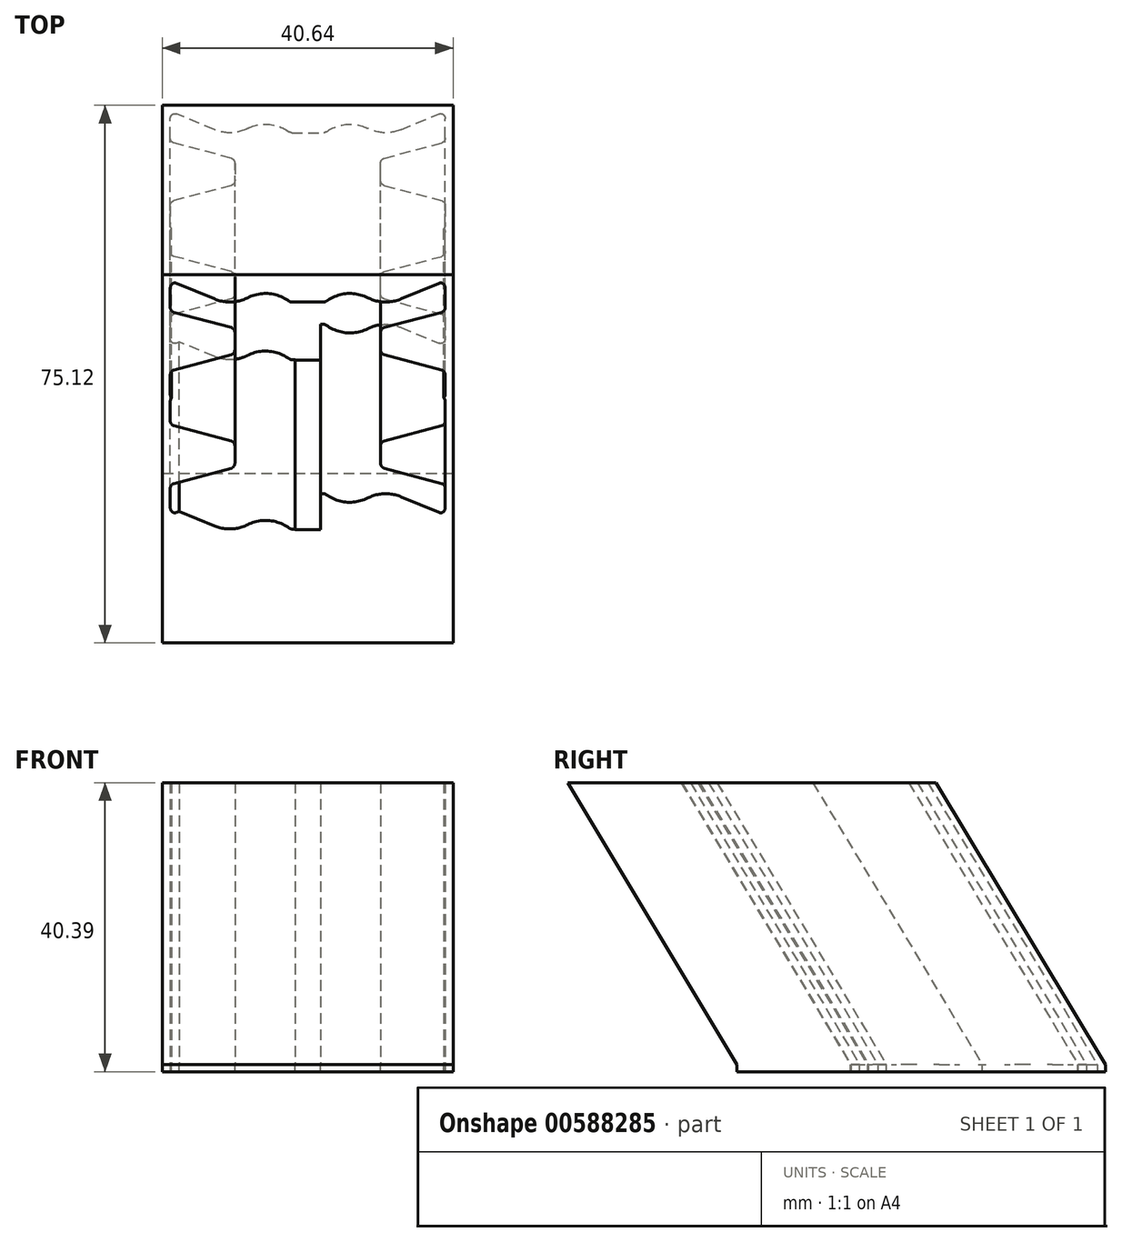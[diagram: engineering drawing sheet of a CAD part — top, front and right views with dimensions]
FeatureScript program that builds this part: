
annotation { "Feature Type Name" : "Feature", "Feature Type Description" : "" }
export const myFeature = defineFeature(function(context is Context, id is Id, definition is map)
    precondition{}
    {
        {
            var Q0;
            Q0=qCreatedBy(makeId("Front.planeOp"),FACE);
            var sketch = newSketch(context, id + "F0", { "sketchPlane" : qUnion([Q0])});
            skLineSegment(sketch, "E0.left", {"start": v(10.18, 1.51) * mm, "end": v(10.18, 0) * mm});
            skLineSegment(sketch, "E1", {"start": v(18.72, 3.46) * mm, "end": v(10.67, 1.62) * mm});
            skLineSegment(sketch, "E2.left", {"start": v(19.2, 6.35) * mm, "end": v(19.22, 4.09) * mm});
            skLineSegment(sketch, "E3", {"start": v(10.18, 1) * mm, "end": v(10.18, 0) * mm});
            skLineSegment(sketch, "E4", {"start": v(18.36, 6.94) * mm, "end": v(13.01, 5.05) * mm});
            skLineSegment(sketch, "E5", {"start": v(1.78, -8.98) * mm, "end": v(1.78, -4.68) * mm});
            skArc(sketch, "E6", {"start": v(8.39, 5.2) * mm, "mid": v(5.43, 5.7) * mm, "end": v(2.57, 4.77) * mm});
            skLineSegment(sketch, "E7", {"start": v(2.42, 4.68) * mm, "end": v(2.42, 4.68) * mm});
            skLineSegment(sketch, "E8.MirrorCS", {"start": v(-1.78, -8.98) * mm, "end": v(-1.78, -4.68) * mm});
            skLineSegment(sketch, "E9", {"start": v(-1.78, -8.98) * mm, "end": v(1.78, -8.98) * mm});
            skPoint(sketch, "E10.visualSharp", {"position": v(10.18, 4.04) * mm});
            skArc(sketch, "E10.filletArc", {"start": v(8.39, 5.2) * mm, "mid": v(10.69, 4.69) * mm, "end": v(13.01, 5.05) * mm});
            skLineSegment(sketch, "E11", {"start": v(0, 4.68) * mm, "end": v(2.23, 4.68) * mm});
            skPoint(sketch, "E12.visualSharp", {"position": v(19.2, 7.24) * mm});
            skArc(sketch, "E12.filletArc", {"start": v(19.2, 6.35) * mm, "mid": v(18.93, 6.86) * mm, "end": v(18.36, 6.94) * mm});
            skPoint(sketch, "E13.visualSharp", {"position": v(19.22, 3.58) * mm});
            skArc(sketch, "E13.filletArc", {"start": v(18.72, 3.46) * mm, "mid": v(19.08, 3.69) * mm, "end": v(19.22, 4.09) * mm});
            skPoint(sketch, "E14.visualSharp", {"position": v(10.18, 1.51) * mm});
            skArc(sketch, "E14.filletArc", {"start": v(10.67, 1.62) * mm, "mid": v(10.31, 1.4) * mm, "end": v(10.18, 1) * mm});
            skPoint(sketch, "E15.visualSharp", {"position": v(2.42, 4.68) * mm});
            skArc(sketch, "E15.filletArc", {"start": v(2.23, 4.68) * mm, "mid": v(2.4, 4.7) * mm, "end": v(2.57, 4.77) * mm});
            skArc(sketch, "E16.MirrorCS", {"start": v(-2.23, 4.68) * mm, "mid": v(-2.4, 4.7) * mm, "end": v(-2.57, 4.77) * mm});
            skLineSegment(sketch, "E17.MirrorCS", {"start": v(-10.18, 1) * mm, "end": v(-10.18, 0) * mm});
            skArc(sketch, "E18.MirrorCS", {"start": v(-10.67, 1.62) * mm, "mid": v(-10.31, 1.4) * mm, "end": v(-10.18, 1) * mm});
            skLineSegment(sketch, "E19.MirrorCS", {"start": v(-19.2, 6.35) * mm, "end": v(-19.22, 4.09) * mm});
            skArc(sketch, "E20.MirrorCS", {"start": v(-18.72, 3.46) * mm, "mid": v(-19.08, 3.69) * mm, "end": v(-19.22, 4.09) * mm});
            skLineSegment(sketch, "E21.MirrorCS", {"start": v(-10.18, 1.51) * mm, "end": v(-10.18, 0) * mm});
            skArc(sketch, "E22.MirrorCS", {"start": v(-19.2, 6.35) * mm, "mid": v(-18.93, 6.86) * mm, "end": v(-18.36, 6.94) * mm});
            skLineSegment(sketch, "E23.MirrorCS", {"start": v(0, 4.68) * mm, "end": v(-2.23, 4.68) * mm});
            skArc(sketch, "E24.MirrorCS", {"start": v(-8.39, 5.2) * mm, "mid": v(-10.69, 4.69) * mm, "end": v(-13.01, 5.05) * mm});
            skPoint(sketch, "E25.MirrorP", {"position": v(-2.42, 4.68) * mm});
            skArc(sketch, "E26.MirrorCS", {"start": v(-8.39, 5.2) * mm, "mid": v(-5.43, 5.7) * mm, "end": v(-2.57, 4.77) * mm});
            skLineSegment(sketch, "E27.MirrorCS", {"start": v(-18.72, 3.46) * mm, "end": v(-10.67, 1.62) * mm});
            skLineSegment(sketch, "E28.MirrorCS", {"start": v(-18.36, 6.94) * mm, "end": v(-13.01, 5.05) * mm});
            skPoint(sketch, "E29.MirrorP", {"position": v(-19.22, 3.58) * mm});
            skPoint(sketch, "E30.MirrorP", {"position": v(-10.18, 1.51) * mm});
            skPoint(sketch, "E31.MirrorP", {"position": v(-10.18, 4.04) * mm});
            skPoint(sketch, "E32.MirrorP", {"position": v(-19.2, 7.24) * mm});
            skLineSegment(sketch, "E33.MirrorCS", {"start": v(-2.42, 4.68) * mm, "end": v(-2.42, 4.68) * mm});
            skLineSegment(sketch, "E34.MirrorCS", {"start": v(10.18, -1.51) * mm, "end": v(10.18, 0) * mm});
            skArc(sketch, "E35.MirrorCS", {"start": v(2.23, -4.68) * mm, "mid": v(2.4, -4.7) * mm, "end": v(2.57, -4.77) * mm});
            skLineSegment(sketch, "E36.MirrorCS", {"start": v(-10.18, -1) * mm, "end": v(-10.18, 0) * mm});
            skArc(sketch, "E37.MirrorCS", {"start": v(-2.23, -4.68) * mm, "mid": v(-2.4, -4.7) * mm, "end": v(-2.57, -4.77) * mm});
            skLineSegment(sketch, "E38.MirrorCS", {"start": v(-19.2, -6.35) * mm, "end": v(-19.22, -4.09) * mm});
            skArc(sketch, "E39.MirrorCS", {"start": v(19.2, -6.35) * mm, "mid": v(18.93, -6.86) * mm, "end": v(18.36, -6.94) * mm});
            skArc(sketch, "E40.MirrorCS", {"start": v(-18.72, -3.46) * mm, "mid": v(-19.08, -3.69) * mm, "end": v(-19.22, -4.09) * mm});
            skLineSegment(sketch, "E41.MirrorCS", {"start": v(10.18, -1) * mm, "end": v(10.18, 0) * mm});
            skArc(sketch, "E42.MirrorCS", {"start": v(10.67, -1.62) * mm, "mid": v(10.31, -1.4) * mm, "end": v(10.18, -1) * mm});
            skLineSegment(sketch, "E43.MirrorCS", {"start": v(19.2, -6.35) * mm, "end": v(19.22, -4.09) * mm});
            skArc(sketch, "E44.MirrorCS", {"start": v(18.72, -3.46) * mm, "mid": v(19.08, -3.69) * mm, "end": v(19.22, -4.09) * mm});
            skArc(sketch, "E45.MirrorCS", {"start": v(-19.2, -6.35) * mm, "mid": v(-18.93, -6.86) * mm, "end": v(-18.36, -6.94) * mm});
            skLineSegment(sketch, "E46.MirrorCS", {"start": v(-10.18, -1.51) * mm, "end": v(-10.18, 0) * mm});
            skArc(sketch, "E47.MirrorCS", {"start": v(-10.67, -1.62) * mm, "mid": v(-10.31, -1.4) * mm, "end": v(-10.18, -1) * mm});
            skLineSegment(sketch, "E48.MirrorCS", {"start": v(1.78, -4.68) * mm, "end": v(2.23, -4.68) * mm});
            skLineSegment(sketch, "E49.MirrorCS", {"start": v(-1.78, -4.68) * mm, "end": v(-2.23, -4.68) * mm});
            skArc(sketch, "E50.MirrorCS", {"start": v(8.39, -5.2) * mm, "mid": v(10.69, -4.69) * mm, "end": v(13.01, -5.05) * mm});
            skArc(sketch, "E51.MirrorCS", {"start": v(-8.39, -5.2) * mm, "mid": v(-10.69, -4.69) * mm, "end": v(-13.01, -5.05) * mm});
            skPoint(sketch, "E52.MirrorP", {"position": v(-2.42, -4.68) * mm});
            skArc(sketch, "E53.MirrorCS", {"start": v(8.39, -5.2) * mm, "mid": v(5.43, -5.7) * mm, "end": v(2.57, -4.77) * mm});
            skPoint(sketch, "E54.MirrorP", {"position": v(2.42, -4.68) * mm});
            skPoint(sketch, "E55.MirrorP", {"position": v(-10.18, -4.04) * mm});
            skPoint(sketch, "E56.MirrorP", {"position": v(19.22, -3.58) * mm});
            skLineSegment(sketch, "E57.MirrorCS", {"start": v(18.72, -3.46) * mm, "end": v(10.67, -1.62) * mm});
            skLineSegment(sketch, "E58.MirrorCS", {"start": v(-18.72, -3.46) * mm, "end": v(-10.67, -1.62) * mm});
            skLineSegment(sketch, "E59.MirrorCS", {"start": v(-18.36, -6.94) * mm, "end": v(-13.01, -5.05) * mm});
            skLineSegment(sketch, "E60.MirrorCS", {"start": v(18.36, -6.94) * mm, "end": v(13.01, -5.05) * mm});
            skPoint(sketch, "E61.MirrorP", {"position": v(19.2, -7.24) * mm});
            skPoint(sketch, "E62.MirrorP", {"position": v(-19.22, -3.58) * mm});
            skArc(sketch, "E63.MirrorCS", {"start": v(-8.39, -5.2) * mm, "mid": v(-5.43, -5.7) * mm, "end": v(-2.57, -4.77) * mm});
            skPoint(sketch, "E64.MirrorP", {"position": v(10.18, -1.51) * mm});
            skPoint(sketch, "E65.MirrorP", {"position": v(-19.2, -7.24) * mm});
            skPoint(sketch, "E66.MirrorP", {"position": v(10.18, -4.04) * mm});
            skPoint(sketch, "E67.MirrorP", {"position": v(-10.18, -1.51) * mm});
            skPoint(sketch, "E68.orphan", {"position": v(0, -4.68) * mm});
            skLineSegment(sketch, "E69.0.1.0", {"start": v(-18.72, 17.05) * mm, "end": v(-10.67, 15.21) * mm});
            skLineSegment(sketch, "E69.0.1.1", {"start": v(-1.78, 4.6) * mm, "end": v(1.78, 4.6) * mm});
            skArc(sketch, "E69.0.1.2", {"start": v(8.39, 18.78) * mm, "mid": v(10.69, 18.27) * mm, "end": v(13.01, 18.64) * mm});
            skLineSegment(sketch, "E69.0.1.3", {"start": v(18.72, 17.05) * mm, "end": v(10.67, 15.21) * mm});
            skPoint(sketch, "E69.0.1.4", {"position": v(10.18, 17.63) * mm});
            skArc(sketch, "E69.0.1.5", {"start": v(-8.39, 8.4) * mm, "mid": v(-5.43, 7.9) * mm, "end": v(-2.57, 8.82) * mm});
            skPoint(sketch, "E69.0.1.6", {"position": v(-10.18, 12.08) * mm});
            skArc(sketch, "E69.0.1.7", {"start": v(-8.39, 18.78) * mm, "mid": v(-5.43, 19.28) * mm, "end": v(-2.57, 18.36) * mm});
            skPoint(sketch, "E69.0.1.8", {"position": v(10.18, 12.08) * mm});
            skArc(sketch, "E69.0.1.9", {"start": v(8.39, 8.4) * mm, "mid": v(10.69, 8.9) * mm, "end": v(13.01, 8.54) * mm});
            skLineSegment(sketch, "E69.0.1.10", {"start": v(-18.36, 6.65) * mm, "end": v(-13.01, 8.54) * mm});
            skArc(sketch, "E69.0.1.11", {"start": v(-8.39, 8.4) * mm, "mid": v(-10.69, 8.9) * mm, "end": v(-13.01, 8.54) * mm});
            skPoint(sketch, "E69.0.1.12", {"position": v(-2.42, 8.91) * mm});
            skLineSegment(sketch, "E69.0.1.13", {"start": v(-18.72, 10.12) * mm, "end": v(-10.67, 11.96) * mm});
            skLineSegment(sketch, "E69.0.1.14", {"start": v(18.72, 10.12) * mm, "end": v(10.67, 11.96) * mm});
            skPoint(sketch, "E69.0.1.15", {"position": v(-19.22, 17.17) * mm});
            skLineSegment(sketch, "E69.0.1.16", {"start": v(18.36, 20.53) * mm, "end": v(13.01, 18.64) * mm});
            skLineSegment(sketch, "E69.0.1.17", {"start": v(1.78, 4.6) * mm, "end": v(1.78, 8.91) * mm});
            skLineSegment(sketch, "E69.0.1.18", {"start": v(-1.78, 4.6) * mm, "end": v(-1.78, 8.91) * mm});
            skLineSegment(sketch, "E69.0.1.19", {"start": v(18.36, 6.65) * mm, "end": v(13.01, 8.54) * mm});
            skPoint(sketch, "E69.0.1.20", {"position": v(10.18, 9.55) * mm});
            skPoint(sketch, "E69.0.1.21", {"position": v(-19.2, 6.35) * mm});
            skPoint(sketch, "E69.0.1.22", {"position": v(0, 8.91) * mm});
            skPoint(sketch, "E69.0.1.23", {"position": v(19.2, 20.83) * mm});
            skArc(sketch, "E69.0.1.24", {"start": v(8.39, 8.4) * mm, "mid": v(5.43, 7.9) * mm, "end": v(2.57, 8.82) * mm});
            skPoint(sketch, "E69.0.1.25", {"position": v(-19.22, 10.01) * mm});
            skPoint(sketch, "E69.0.1.26", {"position": v(-19.2, 20.83) * mm});
            skArc(sketch, "E69.0.1.27", {"start": v(-8.39, 18.78) * mm, "mid": v(-10.69, 18.27) * mm, "end": v(-13.01, 18.64) * mm});
            skPoint(sketch, "E69.0.1.28", {"position": v(19.22, 10.01) * mm});
            skPoint(sketch, "E69.0.1.29", {"position": v(19.22, 17.17) * mm});
            skLineSegment(sketch, "E69.0.1.30", {"start": v(-18.36, 20.53) * mm, "end": v(-13.01, 18.64) * mm});
            skPoint(sketch, "E69.0.1.31", {"position": v(19.2, 6.35) * mm});
            skPoint(sketch, "E69.0.1.32", {"position": v(-10.18, 9.55) * mm});
            skPoint(sketch, "E69.0.1.33", {"position": v(10.18, 15.1) * mm});
            skPoint(sketch, "E69.0.1.34", {"position": v(-10.18, 17.63) * mm});
            skPoint(sketch, "E69.0.1.35", {"position": v(-10.18, 15.1) * mm});
            skPoint(sketch, "E69.0.1.36", {"position": v(2.42, 8.91) * mm});
            skPoint(sketch, "E69.0.1.37", {"position": v(2.42, 18.27) * mm});
            skPoint(sketch, "E69.0.1.38", {"position": v(0, 8.91) * mm});
            skPoint(sketch, "E69.0.1.39", {"position": v(-2.42, 8.91) * mm});
            skPoint(sketch, "E69.0.1.40", {"position": v(10.18, 9.55) * mm});
            skLineSegment(sketch, "E69.0.1.41", {"start": v(18.36, 20.53) * mm, "end": v(13.01, 18.64) * mm});
            skArc(sketch, "E69.0.1.42", {"start": v(8.39, 18.78) * mm, "mid": v(5.43, 19.28) * mm, "end": v(2.57, 18.36) * mm});
            skLineSegment(sketch, "E69.0.1.43", {"start": v(18.72, 17.05) * mm, "end": v(10.67, 15.21) * mm});
            skArc(sketch, "E69.0.1.44", {"start": v(8.39, 18.78) * mm, "mid": v(10.69, 18.27) * mm, "end": v(13.01, 18.64) * mm});
            skArc(sketch, "E69.0.1.45", {"start": v(-8.39, 8.4) * mm, "mid": v(-5.43, 7.9) * mm, "end": v(-2.57, 8.82) * mm});
            skPoint(sketch, "E69.0.1.46", {"position": v(19.2, 6.35) * mm});
            skPoint(sketch, "E69.0.1.47", {"position": v(-2.42, 18.27) * mm});
            skArc(sketch, "E69.0.1.48", {"start": v(8.39, 8.4) * mm, "mid": v(10.69, 8.9) * mm, "end": v(13.01, 8.54) * mm});
            skPoint(sketch, "E69.0.1.49", {"position": v(-10.18, 15.1) * mm});
            skArc(sketch, "E69.0.1.50", {"start": v(8.39, 8.4) * mm, "mid": v(5.43, 7.9) * mm, "end": v(2.57, 8.82) * mm});
            skPoint(sketch, "E69.0.1.51", {"position": v(-10.18, 9.55) * mm});
            skPoint(sketch, "E69.0.1.52", {"position": v(10.18, 17.63) * mm});
            skPoint(sketch, "E69.0.1.53", {"position": v(-10.18, 12.08) * mm});
            skPoint(sketch, "E69.0.1.54", {"position": v(2.42, 8.91) * mm});
            skLineSegment(sketch, "E69.0.1.55", {"start": v(-18.36, 20.53) * mm, "end": v(-13.01, 18.64) * mm});
            skPoint(sketch, "E69.0.1.56", {"position": v(10.18, 15.1) * mm});
            skLineSegment(sketch, "E69.0.1.57", {"start": v(18.36, 6.65) * mm, "end": v(13.01, 8.54) * mm});
            skPoint(sketch, "E69.0.1.58", {"position": v(-19.22, 10.01) * mm});
            skLineSegment(sketch, "E69.0.1.59", {"start": v(-18.72, 17.05) * mm, "end": v(-10.67, 15.21) * mm});
            skLineSegment(sketch, "E69.0.1.60", {"start": v(-18.72, 10.12) * mm, "end": v(-10.67, 11.96) * mm});
            skArc(sketch, "E69.0.1.61", {"start": v(-8.39, 18.78) * mm, "mid": v(-10.69, 18.27) * mm, "end": v(-13.01, 18.64) * mm});
            skArc(sketch, "E69.0.1.62", {"start": v(-8.39, 8.4) * mm, "mid": v(-10.69, 8.9) * mm, "end": v(-13.01, 8.54) * mm});
            skPoint(sketch, "E69.0.1.63", {"position": v(-19.22, 17.17) * mm});
            skPoint(sketch, "E69.0.1.64", {"position": v(19.22, 10.01) * mm});
            skLineSegment(sketch, "E69.0.1.65", {"start": v(-18.36, 6.65) * mm, "end": v(-13.01, 8.54) * mm});
            skPoint(sketch, "E69.0.1.66", {"position": v(19.22, 17.17) * mm});
            skPoint(sketch, "E69.0.1.67", {"position": v(10.18, 12.08) * mm});
            skLineSegment(sketch, "E69.0.1.68", {"start": v(18.72, 10.12) * mm, "end": v(10.67, 11.96) * mm});
            skArc(sketch, "E69.0.1.69", {"start": v(-8.39, 18.78) * mm, "mid": v(-5.43, 19.28) * mm, "end": v(-2.57, 18.36) * mm});
            skPoint(sketch, "E69.0.1.70", {"position": v(-19.2, 20.83) * mm});
            skPoint(sketch, "E69.0.1.71", {"position": v(-10.18, 17.63) * mm});
            skPoint(sketch, "E69.0.1.72", {"position": v(19.2, 20.83) * mm});
            skPoint(sketch, "E69.0.1.73", {"position": v(-19.2, 6.35) * mm});
            skPoint(sketch, "E69.0.1.74", {"position": v(2.42, 18.27) * mm});
            skArc(sketch, "E69.0.1.75", {"start": v(8.39, 18.78) * mm, "mid": v(5.43, 19.28) * mm, "end": v(2.57, 18.36) * mm});
            skPoint(sketch, "E69.0.1.76", {"position": v(0, 8.91) * mm});
            skPoint(sketch, "E69.0.1.77", {"position": v(-2.42, 18.27) * mm});
            skLineSegment(sketch, "E69.0.1.78", {"start": v(0, 18.27) * mm, "end": v(2.23, 18.27) * mm});
            skPoint(sketch, "E69.0.1.79", {"position": v(0, 8.91) * mm});
            skLineSegment(sketch, "E69.0.1.80", {"start": v(0, 18.27) * mm, "end": v(-2.23, 18.27) * mm});
            skLineSegment(sketch, "E69.0.1.81", {"start": v(-19.2, 19.93) * mm, "end": v(-19.22, 17.68) * mm});
            skArc(sketch, "E69.0.1.82", {"start": v(-19.2, 7.24) * mm, "mid": v(-18.93, 6.73) * mm, "end": v(-18.36, 6.65) * mm});
            skLineSegment(sketch, "E69.0.1.83", {"start": v(19.2, 7.24) * mm, "end": v(19.22, 9.5) * mm});
            skLineSegment(sketch, "E69.0.1.84", {"start": v(0, 18.27) * mm, "end": v(-2.23, 18.27) * mm});
            skArc(sketch, "E69.0.1.85", {"start": v(-19.2, 19.93) * mm, "mid": v(-18.93, 20.45) * mm, "end": v(-18.36, 20.53) * mm});
            skLineSegment(sketch, "E69.0.1.86", {"start": v(-19.2, 7.24) * mm, "end": v(-19.22, 9.5) * mm});
            skArc(sketch, "E69.0.1.87", {"start": v(19.2, 7.24) * mm, "mid": v(18.93, 6.73) * mm, "end": v(18.36, 6.65) * mm});
            skLineSegment(sketch, "E69.0.1.88", {"start": v(0, 18.27) * mm, "end": v(2.23, 18.27) * mm});
            skLineSegment(sketch, "E69.0.1.89", {"start": v(-19.2, 19.93) * mm, "end": v(-19.22, 17.68) * mm});
            skArc(sketch, "E69.0.1.90", {"start": v(19.2, 19.93) * mm, "mid": v(18.93, 20.45) * mm, "end": v(18.36, 20.53) * mm});
            skLineSegment(sketch, "E69.0.1.91", {"start": v(19.2, 19.93) * mm, "end": v(19.22, 17.68) * mm});
            skArc(sketch, "E69.0.1.92", {"start": v(-19.2, 19.93) * mm, "mid": v(-18.93, 20.45) * mm, "end": v(-18.36, 20.53) * mm});
            skLineSegment(sketch, "E69.0.1.93", {"start": v(-19.2, 7.24) * mm, "end": v(-19.22, 9.5) * mm});
            skLineSegment(sketch, "E69.0.1.94", {"start": v(19.2, 7.24) * mm, "end": v(19.22, 9.5) * mm});
            skArc(sketch, "E69.0.1.95", {"start": v(-19.2, 7.24) * mm, "mid": v(-18.93, 6.73) * mm, "end": v(-18.36, 6.65) * mm});
            skArc(sketch, "E69.0.1.96", {"start": v(19.2, 7.24) * mm, "mid": v(18.93, 6.73) * mm, "end": v(18.36, 6.65) * mm});
            skArc(sketch, "E69.0.1.97", {"start": v(18.72, 10.12) * mm, "mid": v(19.08, 9.9) * mm, "end": v(19.22, 9.5) * mm});
            skLineSegment(sketch, "E69.0.1.98", {"start": v(-10.18, 15.1) * mm, "end": v(-10.18, 13.59) * mm});
            skLineSegment(sketch, "E69.0.1.99", {"start": v(10.18, 12.08) * mm, "end": v(10.18, 13.59) * mm});
            skLineSegment(sketch, "E69.0.1.100", {"start": v(10.18, 15.1) * mm, "end": v(10.18, 13.59) * mm});
            skArc(sketch, "E69.0.1.101", {"start": v(2.23, 8.91) * mm, "mid": v(2.4, 8.89) * mm, "end": v(2.57, 8.82) * mm});
            skArc(sketch, "E69.0.1.102", {"start": v(10.67, 11.96) * mm, "mid": v(10.31, 12.19) * mm, "end": v(10.18, 12.58) * mm});
            skArc(sketch, "E69.0.1.103", {"start": v(-18.72, 17.05) * mm, "mid": v(-19.08, 17.28) * mm, "end": v(-19.22, 17.68) * mm});
            skLineSegment(sketch, "E69.0.1.104", {"start": v(1.78, 8.91) * mm, "end": v(2.23, 8.91) * mm});
            skLineSegment(sketch, "E69.0.1.105", {"start": v(19.2, 19.93) * mm, "end": v(19.22, 17.68) * mm});
            skArc(sketch, "E69.0.1.106", {"start": v(-2.23, 8.91) * mm, "mid": v(-2.4, 8.89) * mm, "end": v(-2.57, 8.82) * mm});
            skArc(sketch, "E69.0.1.107", {"start": v(18.72, 17.05) * mm, "mid": v(19.08, 17.28) * mm, "end": v(19.22, 17.68) * mm});
            skArc(sketch, "E69.0.1.108", {"start": v(10.67, 15.21) * mm, "mid": v(10.31, 15) * mm, "end": v(10.18, 14.6) * mm});
            skLineSegment(sketch, "E69.0.1.109", {"start": v(-1.78, 8.91) * mm, "end": v(-2.23, 8.91) * mm});
            skArc(sketch, "E69.0.1.110", {"start": v(-10.67, 15.21) * mm, "mid": v(-10.31, 15) * mm, "end": v(-10.18, 14.6) * mm});
            skArc(sketch, "E69.0.1.111", {"start": v(-18.72, 10.12) * mm, "mid": v(-19.08, 9.9) * mm, "end": v(-19.22, 9.5) * mm});
            skArc(sketch, "E69.0.1.112", {"start": v(19.2, 19.93) * mm, "mid": v(18.93, 20.45) * mm, "end": v(18.36, 20.53) * mm});
            skArc(sketch, "E69.0.1.113", {"start": v(10.67, 15.21) * mm, "mid": v(10.31, 15) * mm, "end": v(10.18, 14.6) * mm});
            skArc(sketch, "E69.0.1.114", {"start": v(-10.67, 11.96) * mm, "mid": v(-10.31, 12.19) * mm, "end": v(-10.18, 12.58) * mm});
            skArc(sketch, "E69.0.1.115", {"start": v(-2.23, 18.27) * mm, "mid": v(-2.4, 18.3) * mm, "end": v(-2.57, 18.36) * mm});
            skLineSegment(sketch, "E69.0.1.116", {"start": v(10.18, 15.1) * mm, "end": v(10.18, 13.59) * mm});
            skLineSegment(sketch, "E69.0.1.117", {"start": v(-1.78, 8.91) * mm, "end": v(-2.23, 8.91) * mm});
            skLineSegment(sketch, "E69.0.1.118", {"start": v(1.78, 8.91) * mm, "end": v(2.23, 8.91) * mm});
            skArc(sketch, "E69.0.1.119", {"start": v(-10.67, 15.21) * mm, "mid": v(-10.31, 15) * mm, "end": v(-10.18, 14.6) * mm});
            skArc(sketch, "E69.0.1.120", {"start": v(2.23, 18.27) * mm, "mid": v(2.4, 18.3) * mm, "end": v(2.57, 18.36) * mm});
            skArc(sketch, "E69.0.1.121", {"start": v(-18.72, 17.05) * mm, "mid": v(-19.08, 17.28) * mm, "end": v(-19.22, 17.68) * mm});
            skLineSegment(sketch, "E69.0.1.122", {"start": v(-10.18, 12.08) * mm, "end": v(-10.18, 13.59) * mm});
            skArc(sketch, "E69.0.1.123", {"start": v(18.72, 10.12) * mm, "mid": v(19.08, 9.9) * mm, "end": v(19.22, 9.5) * mm});
            skLineSegment(sketch, "E69.0.1.124", {"start": v(10.18, 12.58) * mm, "end": v(10.18, 13.59) * mm});
            skLineSegment(sketch, "E69.0.1.125", {"start": v(-10.18, 15.1) * mm, "end": v(-10.18, 13.59) * mm});
            skArc(sketch, "E69.0.1.126", {"start": v(-2.23, 8.91) * mm, "mid": v(-2.4, 8.89) * mm, "end": v(-2.57, 8.82) * mm});
            skArc(sketch, "E69.0.1.127", {"start": v(10.67, 11.96) * mm, "mid": v(10.31, 12.19) * mm, "end": v(10.18, 12.58) * mm});
            skArc(sketch, "E69.0.1.128", {"start": v(-18.72, 10.12) * mm, "mid": v(-19.08, 9.9) * mm, "end": v(-19.22, 9.5) * mm});
            skArc(sketch, "E69.0.1.129", {"start": v(18.72, 17.05) * mm, "mid": v(19.08, 17.28) * mm, "end": v(19.22, 17.68) * mm});
            skArc(sketch, "E69.0.1.130", {"start": v(2.23, 8.91) * mm, "mid": v(2.4, 8.89) * mm, "end": v(2.57, 8.82) * mm});
            skLineSegment(sketch, "E69.0.1.131", {"start": v(10.18, 12.08) * mm, "end": v(10.18, 13.59) * mm});
            skLineSegment(sketch, "E69.0.1.132", {"start": v(-10.18, 12.08) * mm, "end": v(-10.18, 13.59) * mm});
            skLineSegment(sketch, "E69.0.1.133", {"start": v(10.18, 12.58) * mm, "end": v(10.18, 13.59) * mm});
            skArc(sketch, "E69.0.1.134", {"start": v(-10.67, 11.96) * mm, "mid": v(-10.31, 12.19) * mm, "end": v(-10.18, 12.58) * mm});
            skArc(sketch, "E69.0.1.135", {"start": v(-2.23, 18.27) * mm, "mid": v(-2.4, 18.3) * mm, "end": v(-2.57, 18.36) * mm});
            skArc(sketch, "E69.0.1.136", {"start": v(2.23, 18.27) * mm, "mid": v(2.4, 18.3) * mm, "end": v(2.57, 18.36) * mm});
            skLineSegment(sketch, "E69.0.1.137", {"start": v(-10.18, 14.6) * mm, "end": v(-10.18, 13.59) * mm});
            skLineSegment(sketch, "E69.0.1.138", {"start": v(-10.18, 12.58) * mm, "end": v(-10.18, 13.59) * mm});
            skLineSegment(sketch, "E69.0.1.139", {"start": v(10.18, 14.6) * mm, "end": v(10.18, 13.59) * mm});
            skLineSegment(sketch, "E69.0.1.140", {"start": v(-10.18, 14.6) * mm, "end": v(-10.18, 13.59) * mm});
            skLineSegment(sketch, "E69.0.1.141", {"start": v(-10.18, 12.58) * mm, "end": v(-10.18, 13.59) * mm});
            skLineSegment(sketch, "E69.0.1.142", {"start": v(10.18, 14.6) * mm, "end": v(10.18, 13.59) * mm});
            skLineSegment(sketch, "E69.0.2.0", {"start": v(-18.72, 30.64) * mm, "end": v(-10.67, 28.8) * mm});
            skLineSegment(sketch, "E69.0.2.1", {"start": v(-1.78, 18.2) * mm, "end": v(1.78, 18.2) * mm});
            skArc(sketch, "E69.0.2.2", {"start": v(8.39, 32.37) * mm, "mid": v(10.69, 31.86) * mm, "end": v(13.01, 32.22) * mm});
            skLineSegment(sketch, "E69.0.2.3", {"start": v(18.72, 30.64) * mm, "end": v(10.67, 28.8) * mm});
            skPoint(sketch, "E69.0.2.4", {"position": v(10.18, 31.22) * mm});
            skArc(sketch, "E69.0.2.5", {"start": v(-8.39, 21.98) * mm, "mid": v(-5.43, 21.49) * mm, "end": v(-2.57, 22.4) * mm});
            skPoint(sketch, "E69.0.2.6", {"position": v(-10.18, 25.67) * mm});
            skArc(sketch, "E69.0.2.7", {"start": v(-8.39, 32.37) * mm, "mid": v(-5.43, 32.87) * mm, "end": v(-2.57, 31.95) * mm});
            skPoint(sketch, "E69.0.2.8", {"position": v(10.18, 25.67) * mm});
            skArc(sketch, "E69.0.2.9", {"start": v(8.39, 21.98) * mm, "mid": v(10.69, 22.5) * mm, "end": v(13.01, 22.13) * mm});
            skLineSegment(sketch, "E69.0.2.10", {"start": v(-18.36, 20.24) * mm, "end": v(-13.01, 22.13) * mm});
            skArc(sketch, "E69.0.2.11", {"start": v(-8.39, 21.98) * mm, "mid": v(-10.69, 22.5) * mm, "end": v(-13.01, 22.13) * mm});
            skPoint(sketch, "E69.0.2.12", {"position": v(-2.42, 22.5) * mm});
            skLineSegment(sketch, "E69.0.2.13", {"start": v(-18.72, 23.71) * mm, "end": v(-10.67, 25.55) * mm});
            skLineSegment(sketch, "E69.0.2.14", {"start": v(18.72, 23.71) * mm, "end": v(10.67, 25.55) * mm});
            skPoint(sketch, "E69.0.2.15", {"position": v(-19.22, 30.76) * mm});
            skLineSegment(sketch, "E69.0.2.16", {"start": v(18.36, 34.12) * mm, "end": v(13.01, 32.22) * mm});
            skLineSegment(sketch, "E69.0.2.17", {"start": v(1.78, 18.2) * mm, "end": v(1.78, 22.5) * mm});
            skLineSegment(sketch, "E69.0.2.18", {"start": v(-1.78, 18.2) * mm, "end": v(-1.78, 22.5) * mm});
            skLineSegment(sketch, "E69.0.2.19", {"start": v(18.36, 20.24) * mm, "end": v(13.01, 22.13) * mm});
            skPoint(sketch, "E69.0.2.20", {"position": v(10.18, 23.14) * mm});
            skPoint(sketch, "E69.0.2.21", {"position": v(-19.2, 19.94) * mm});
            skPoint(sketch, "E69.0.2.22", {"position": v(0, 22.5) * mm});
            skPoint(sketch, "E69.0.2.23", {"position": v(19.2, 34.42) * mm});
            skArc(sketch, "E69.0.2.24", {"start": v(8.39, 21.98) * mm, "mid": v(5.43, 21.49) * mm, "end": v(2.57, 22.4) * mm});
            skPoint(sketch, "E69.0.2.25", {"position": v(-19.22, 23.6) * mm});
            skPoint(sketch, "E69.0.2.26", {"position": v(-19.2, 34.42) * mm});
            skArc(sketch, "E69.0.2.27", {"start": v(-8.39, 32.37) * mm, "mid": v(-10.69, 31.86) * mm, "end": v(-13.01, 32.22) * mm});
            skPoint(sketch, "E69.0.2.28", {"position": v(19.22, 23.6) * mm});
            skPoint(sketch, "E69.0.2.29", {"position": v(19.22, 30.76) * mm});
            skLineSegment(sketch, "E69.0.2.30", {"start": v(-18.36, 34.12) * mm, "end": v(-13.01, 32.22) * mm});
            skPoint(sketch, "E69.0.2.31", {"position": v(19.2, 19.94) * mm});
            skPoint(sketch, "E69.0.2.32", {"position": v(-10.18, 23.14) * mm});
            skPoint(sketch, "E69.0.2.33", {"position": v(10.18, 28.69) * mm});
            skPoint(sketch, "E69.0.2.34", {"position": v(-10.18, 31.22) * mm});
            skPoint(sketch, "E69.0.2.35", {"position": v(-10.18, 28.69) * mm});
            skPoint(sketch, "E69.0.2.36", {"position": v(2.42, 22.5) * mm});
            skPoint(sketch, "E69.0.2.37", {"position": v(2.42, 31.86) * mm});
            skPoint(sketch, "E69.0.2.38", {"position": v(0, 22.5) * mm});
            skPoint(sketch, "E69.0.2.39", {"position": v(-2.42, 22.5) * mm});
            skPoint(sketch, "E69.0.2.40", {"position": v(10.18, 23.14) * mm});
            skLineSegment(sketch, "E69.0.2.41", {"start": v(18.36, 34.12) * mm, "end": v(13.01, 32.22) * mm});
            skArc(sketch, "E69.0.2.42", {"start": v(8.39, 32.37) * mm, "mid": v(5.43, 32.87) * mm, "end": v(2.57, 31.95) * mm});
            skLineSegment(sketch, "E69.0.2.43", {"start": v(18.72, 30.64) * mm, "end": v(10.67, 28.8) * mm});
            skArc(sketch, "E69.0.2.44", {"start": v(8.39, 32.37) * mm, "mid": v(10.69, 31.86) * mm, "end": v(13.01, 32.22) * mm});
            skArc(sketch, "E69.0.2.45", {"start": v(-8.39, 21.98) * mm, "mid": v(-5.43, 21.49) * mm, "end": v(-2.57, 22.4) * mm});
            skPoint(sketch, "E69.0.2.46", {"position": v(19.2, 19.94) * mm});
            skPoint(sketch, "E69.0.2.47", {"position": v(-2.42, 31.86) * mm});
            skArc(sketch, "E69.0.2.48", {"start": v(8.39, 21.98) * mm, "mid": v(10.69, 22.5) * mm, "end": v(13.01, 22.13) * mm});
            skPoint(sketch, "E69.0.2.49", {"position": v(-10.18, 28.69) * mm});
            skArc(sketch, "E69.0.2.50", {"start": v(8.39, 21.98) * mm, "mid": v(5.43, 21.49) * mm, "end": v(2.57, 22.4) * mm});
            skPoint(sketch, "E69.0.2.51", {"position": v(-10.18, 23.14) * mm});
            skPoint(sketch, "E69.0.2.52", {"position": v(10.18, 31.22) * mm});
            skPoint(sketch, "E69.0.2.53", {"position": v(-10.18, 25.67) * mm});
            skPoint(sketch, "E69.0.2.54", {"position": v(2.42, 22.5) * mm});
            skLineSegment(sketch, "E69.0.2.55", {"start": v(-18.36, 34.12) * mm, "end": v(-13.01, 32.22) * mm});
            skPoint(sketch, "E69.0.2.56", {"position": v(10.18, 28.69) * mm});
            skLineSegment(sketch, "E69.0.2.57", {"start": v(18.36, 20.24) * mm, "end": v(13.01, 22.13) * mm});
            skPoint(sketch, "E69.0.2.58", {"position": v(-19.22, 23.6) * mm});
            skLineSegment(sketch, "E69.0.2.59", {"start": v(-18.72, 30.64) * mm, "end": v(-10.67, 28.8) * mm});
            skLineSegment(sketch, "E69.0.2.60", {"start": v(-18.72, 23.71) * mm, "end": v(-10.67, 25.55) * mm});
            skArc(sketch, "E69.0.2.61", {"start": v(-8.39, 32.37) * mm, "mid": v(-10.69, 31.86) * mm, "end": v(-13.01, 32.22) * mm});
            skArc(sketch, "E69.0.2.62", {"start": v(-8.39, 21.98) * mm, "mid": v(-10.69, 22.5) * mm, "end": v(-13.01, 22.13) * mm});
            skPoint(sketch, "E69.0.2.63", {"position": v(-19.22, 30.76) * mm});
            skPoint(sketch, "E69.0.2.64", {"position": v(19.22, 23.6) * mm});
            skLineSegment(sketch, "E69.0.2.65", {"start": v(-18.36, 20.24) * mm, "end": v(-13.01, 22.13) * mm});
            skPoint(sketch, "E69.0.2.66", {"position": v(19.22, 30.76) * mm});
            skPoint(sketch, "E69.0.2.67", {"position": v(10.18, 25.67) * mm});
            skLineSegment(sketch, "E69.0.2.68", {"start": v(18.72, 23.71) * mm, "end": v(10.67, 25.55) * mm});
            skArc(sketch, "E69.0.2.69", {"start": v(-8.39, 32.37) * mm, "mid": v(-5.43, 32.87) * mm, "end": v(-2.57, 31.95) * mm});
            skPoint(sketch, "E69.0.2.70", {"position": v(-19.2, 34.42) * mm});
            skPoint(sketch, "E69.0.2.71", {"position": v(-10.18, 31.22) * mm});
            skPoint(sketch, "E69.0.2.72", {"position": v(19.2, 34.42) * mm});
            skPoint(sketch, "E69.0.2.73", {"position": v(-19.2, 19.94) * mm});
            skPoint(sketch, "E69.0.2.74", {"position": v(2.42, 31.86) * mm});
            skArc(sketch, "E69.0.2.75", {"start": v(8.39, 32.37) * mm, "mid": v(5.43, 32.87) * mm, "end": v(2.57, 31.95) * mm});
            skPoint(sketch, "E69.0.2.76", {"position": v(0, 22.5) * mm});
            skPoint(sketch, "E69.0.2.77", {"position": v(-2.42, 31.86) * mm});
            skLineSegment(sketch, "E69.0.2.78", {"start": v(0, 31.86) * mm, "end": v(2.23, 31.86) * mm});
            skPoint(sketch, "E69.0.2.79", {"position": v(0, 22.5) * mm});
            skLineSegment(sketch, "E69.0.2.80", {"start": v(0, 31.86) * mm, "end": v(-2.23, 31.86) * mm});
            skLineSegment(sketch, "E69.0.2.81", {"start": v(-19.2, 33.52) * mm, "end": v(-19.22, 31.27) * mm});
            skArc(sketch, "E69.0.2.82", {"start": v(-19.2, 20.83) * mm, "mid": v(-18.93, 20.32) * mm, "end": v(-18.36, 20.24) * mm});
            skLineSegment(sketch, "E69.0.2.83", {"start": v(19.2, 20.83) * mm, "end": v(19.22, 23.1) * mm});
            skLineSegment(sketch, "E69.0.2.84", {"start": v(0, 31.86) * mm, "end": v(-2.23, 31.86) * mm});
            skArc(sketch, "E69.0.2.85", {"start": v(-19.2, 33.52) * mm, "mid": v(-18.93, 34.04) * mm, "end": v(-18.36, 34.12) * mm});
            skLineSegment(sketch, "E69.0.2.86", {"start": v(-19.2, 20.83) * mm, "end": v(-19.22, 23.1) * mm});
            skArc(sketch, "E69.0.2.87", {"start": v(19.2, 20.83) * mm, "mid": v(18.93, 20.32) * mm, "end": v(18.36, 20.24) * mm});
            skLineSegment(sketch, "E69.0.2.88", {"start": v(0, 31.86) * mm, "end": v(2.23, 31.86) * mm});
            skLineSegment(sketch, "E69.0.2.89", {"start": v(-19.2, 33.52) * mm, "end": v(-19.22, 31.27) * mm});
            skArc(sketch, "E69.0.2.90", {"start": v(19.2, 33.52) * mm, "mid": v(18.93, 34.04) * mm, "end": v(18.36, 34.12) * mm});
            skLineSegment(sketch, "E69.0.2.91", {"start": v(19.2, 33.52) * mm, "end": v(19.22, 31.27) * mm});
            skArc(sketch, "E69.0.2.92", {"start": v(-19.2, 33.52) * mm, "mid": v(-18.93, 34.04) * mm, "end": v(-18.36, 34.12) * mm});
            skLineSegment(sketch, "E69.0.2.93", {"start": v(-19.2, 20.83) * mm, "end": v(-19.22, 23.1) * mm});
            skLineSegment(sketch, "E69.0.2.94", {"start": v(19.2, 20.83) * mm, "end": v(19.22, 23.1) * mm});
            skArc(sketch, "E69.0.2.95", {"start": v(-19.2, 20.83) * mm, "mid": v(-18.93, 20.32) * mm, "end": v(-18.36, 20.24) * mm});
            skArc(sketch, "E69.0.2.96", {"start": v(19.2, 20.83) * mm, "mid": v(18.93, 20.32) * mm, "end": v(18.36, 20.24) * mm});
            skArc(sketch, "E69.0.2.97", {"start": v(18.72, 23.71) * mm, "mid": v(19.08, 23.49) * mm, "end": v(19.22, 23.1) * mm});
            skLineSegment(sketch, "E69.0.2.98", {"start": v(-10.18, 28.69) * mm, "end": v(-10.18, 27.18) * mm});
            skLineSegment(sketch, "E69.0.2.99", {"start": v(10.18, 25.67) * mm, "end": v(10.18, 27.18) * mm});
            skLineSegment(sketch, "E69.0.2.100", {"start": v(10.18, 28.69) * mm, "end": v(10.18, 27.18) * mm});
            skArc(sketch, "E69.0.2.101", {"start": v(2.23, 22.5) * mm, "mid": v(2.4, 22.48) * mm, "end": v(2.57, 22.4) * mm});
            skArc(sketch, "E69.0.2.102", {"start": v(10.67, 25.55) * mm, "mid": v(10.31, 25.78) * mm, "end": v(10.18, 26.17) * mm});
            skArc(sketch, "E69.0.2.103", {"start": v(-18.72, 30.64) * mm, "mid": v(-19.08, 30.87) * mm, "end": v(-19.22, 31.27) * mm});
            skLineSegment(sketch, "E69.0.2.104", {"start": v(1.78, 22.5) * mm, "end": v(2.23, 22.5) * mm});
            skLineSegment(sketch, "E69.0.2.105", {"start": v(19.2, 33.52) * mm, "end": v(19.22, 31.27) * mm});
            skArc(sketch, "E69.0.2.106", {"start": v(-2.23, 22.5) * mm, "mid": v(-2.4, 22.48) * mm, "end": v(-2.57, 22.4) * mm});
            skArc(sketch, "E69.0.2.107", {"start": v(18.72, 30.64) * mm, "mid": v(19.08, 30.87) * mm, "end": v(19.22, 31.27) * mm});
            skArc(sketch, "E69.0.2.108", {"start": v(10.67, 28.8) * mm, "mid": v(10.31, 28.58) * mm, "end": v(10.18, 28.18) * mm});
            skLineSegment(sketch, "E69.0.2.109", {"start": v(-1.78, 22.5) * mm, "end": v(-2.23, 22.5) * mm});
            skArc(sketch, "E69.0.2.110", {"start": v(-10.67, 28.8) * mm, "mid": v(-10.31, 28.58) * mm, "end": v(-10.18, 28.18) * mm});
            skArc(sketch, "E69.0.2.111", {"start": v(-18.72, 23.71) * mm, "mid": v(-19.08, 23.49) * mm, "end": v(-19.22, 23.1) * mm});
            skArc(sketch, "E69.0.2.112", {"start": v(19.2, 33.52) * mm, "mid": v(18.93, 34.04) * mm, "end": v(18.36, 34.12) * mm});
            skArc(sketch, "E69.0.2.113", {"start": v(10.67, 28.8) * mm, "mid": v(10.31, 28.58) * mm, "end": v(10.18, 28.18) * mm});
            skArc(sketch, "E69.0.2.114", {"start": v(-10.67, 25.55) * mm, "mid": v(-10.31, 25.78) * mm, "end": v(-10.18, 26.17) * mm});
            skArc(sketch, "E69.0.2.115", {"start": v(-2.23, 31.86) * mm, "mid": v(-2.4, 31.88) * mm, "end": v(-2.57, 31.95) * mm});
            skLineSegment(sketch, "E69.0.2.116", {"start": v(10.18, 28.69) * mm, "end": v(10.18, 27.18) * mm});
            skLineSegment(sketch, "E69.0.2.117", {"start": v(-1.78, 22.5) * mm, "end": v(-2.23, 22.5) * mm});
            skLineSegment(sketch, "E69.0.2.118", {"start": v(1.78, 22.5) * mm, "end": v(2.23, 22.5) * mm});
            skArc(sketch, "E69.0.2.119", {"start": v(-10.67, 28.8) * mm, "mid": v(-10.31, 28.58) * mm, "end": v(-10.18, 28.18) * mm});
            skArc(sketch, "E69.0.2.120", {"start": v(2.23, 31.86) * mm, "mid": v(2.4, 31.88) * mm, "end": v(2.57, 31.95) * mm});
            skArc(sketch, "E69.0.2.121", {"start": v(-18.72, 30.64) * mm, "mid": v(-19.08, 30.87) * mm, "end": v(-19.22, 31.27) * mm});
            skLineSegment(sketch, "E69.0.2.122", {"start": v(-10.18, 25.67) * mm, "end": v(-10.18, 27.18) * mm});
            skArc(sketch, "E69.0.2.123", {"start": v(18.72, 23.71) * mm, "mid": v(19.08, 23.49) * mm, "end": v(19.22, 23.1) * mm});
            skLineSegment(sketch, "E69.0.2.124", {"start": v(10.18, 26.17) * mm, "end": v(10.18, 27.18) * mm});
            skLineSegment(sketch, "E69.0.2.125", {"start": v(-10.18, 28.69) * mm, "end": v(-10.18, 27.18) * mm});
            skArc(sketch, "E69.0.2.126", {"start": v(-2.23, 22.5) * mm, "mid": v(-2.4, 22.48) * mm, "end": v(-2.57, 22.4) * mm});
            skArc(sketch, "E69.0.2.127", {"start": v(10.67, 25.55) * mm, "mid": v(10.31, 25.78) * mm, "end": v(10.18, 26.17) * mm});
            skArc(sketch, "E69.0.2.128", {"start": v(-18.72, 23.71) * mm, "mid": v(-19.08, 23.49) * mm, "end": v(-19.22, 23.1) * mm});
            skArc(sketch, "E69.0.2.129", {"start": v(18.72, 30.64) * mm, "mid": v(19.08, 30.87) * mm, "end": v(19.22, 31.27) * mm});
            skArc(sketch, "E69.0.2.130", {"start": v(2.23, 22.5) * mm, "mid": v(2.4, 22.48) * mm, "end": v(2.57, 22.4) * mm});
            skLineSegment(sketch, "E69.0.2.131", {"start": v(10.18, 25.67) * mm, "end": v(10.18, 27.18) * mm});
            skLineSegment(sketch, "E69.0.2.132", {"start": v(-10.18, 25.67) * mm, "end": v(-10.18, 27.18) * mm});
            skLineSegment(sketch, "E69.0.2.133", {"start": v(10.18, 26.17) * mm, "end": v(10.18, 27.18) * mm});
            skArc(sketch, "E69.0.2.134", {"start": v(-10.67, 25.55) * mm, "mid": v(-10.31, 25.78) * mm, "end": v(-10.18, 26.17) * mm});
            skArc(sketch, "E69.0.2.135", {"start": v(-2.23, 31.86) * mm, "mid": v(-2.4, 31.88) * mm, "end": v(-2.57, 31.95) * mm});
            skArc(sketch, "E69.0.2.136", {"start": v(2.23, 31.86) * mm, "mid": v(2.4, 31.88) * mm, "end": v(2.57, 31.95) * mm});
            skLineSegment(sketch, "E69.0.2.137", {"start": v(-10.18, 28.18) * mm, "end": v(-10.18, 27.18) * mm});
            skLineSegment(sketch, "E69.0.2.138", {"start": v(-10.18, 26.17) * mm, "end": v(-10.18, 27.18) * mm});
            skLineSegment(sketch, "E69.0.2.139", {"start": v(10.18, 28.18) * mm, "end": v(10.18, 27.18) * mm});
            skLineSegment(sketch, "E69.0.2.140", {"start": v(-10.18, 28.18) * mm, "end": v(-10.18, 27.18) * mm});
            skLineSegment(sketch, "E69.0.2.141", {"start": v(-10.18, 26.17) * mm, "end": v(-10.18, 27.18) * mm});
            skLineSegment(sketch, "E69.0.2.142", {"start": v(10.18, 28.18) * mm, "end": v(10.18, 27.18) * mm});
            skLineSegment(sketch, "E69.direction1", {"start": v(-19.2, -7.24) * mm, "end": v(17.12, -7.24) * mm, "construction": true});
            skLineSegment(sketch, "E69.direction2", {"start": v(-19.2, -7.24) * mm, "end": v(-19.2, 6.35) * mm, "construction": true});
            skLineSegment(sketch, "E70.bottom", {"start": v(-20.32, 35.13) * mm, "end": v(20.32, 35.13) * mm});
            skLineSegment(sketch, "E70.top", {"start": v(-20.32, -8.98) * mm, "end": v(20.32, -8.98) * mm});
            skLineSegment(sketch, "E70.left", {"start": v(-20.32, 35.13) * mm, "end": v(-20.32, -8.98) * mm});
            skLineSegment(sketch, "E70.right", {"start": v(20.32, 35.13) * mm, "end": v(20.32, -8.98) * mm});
            skSolve(sketch);
        }
        {
            var Q0;
            {var subQ6=sQuery(id+"F0.wireOp",EDGE,"E69.0.1.61");Q0=makeQuery(id+"F0.imprint","IMPRINT",FACE,{"disambiguationData":[TD([[makeQuery(id+"F0.imprint","IMPRINT",EDGE,{"derivedFrom":subQ6}),-1.0]])]});}
            var Q1;
            {var subQ2=sQuery(id+"F0.wireOp",EDGE,"E69.0.1.44");Q1=makeQuery(id+"F0.imprint","IMPRINT",FACE,{"disambiguationData":[TD([[makeQuery(id+"F0.imprint","IMPRINT",EDGE,{"derivedFrom":subQ2}),1.0]])]});}
            var Q2;
            {var subQ6=sQuery(id+"F0.wireOp",EDGE,"E15.filletArc");Q2=makeQuery(id+"F0.imprint","IMPRINT",FACE,{"disambiguationData":[TD([[makeQuery(id+"F0.imprint","IMPRINT",EDGE,{"derivedFrom":subQ6}),1.0]])]});}
            var Q3;
            {var subQ5=sQuery(id+"F0.wireOp",EDGE,"E16.MirrorCS");Q3=makeQuery(id+"F0.imprint","IMPRINT",FACE,{"disambiguationData":[TD([[makeQuery(id+"F0.imprint","IMPRINT",EDGE,{"derivedFrom":subQ5}),-1.0]])]});}
            var Q4;
            {var subQ14=sQuery(id+"F0.wireOp",EDGE,"E5");Q4=makeQuery(id+"F0.imprint","IMPRINT",FACE,{"disambiguationData":[TD([[makeQuery(id+"F0.imprint","IMPRINT",EDGE,{"derivedFrom":subQ14}),-1.0]])]});}
            extrude(context, id + "F1", {"entities" : qUnion([Q0, Q1, Q2, Q3, Q4]), "depth" : 88.9 * mm, "offsetDistance" : 25.4 * mm});
        }
        {
            var Q0;
            Q0=makeQuery(id+"F1.opExtrude","SWEPT_BODY",BODY,{"disambiguationData":[OSD([sQuery(id+"F0.wireOp",EDGE,"E5"),sQuery(id+"F0.wireOp",EDGE,"E8.MirrorCS"),sQuery(id+"F0.wireOp",EDGE,"E17.MirrorCS"),sQuery(id+"F0.wireOp",EDGE,"E18.MirrorCS"),sQuery(id+"F0.wireOp",EDGE,"E14.filletArc"),sQuery(id+"F0.wireOp",EDGE,"E20.MirrorCS"),sQuery(id+"F0.wireOp",EDGE,"E19.MirrorCS"),sQuery(id+"F0.wireOp",EDGE,"E3"),sQuery(id+"F0.wireOp",EDGE,"E2.left"),sQuery(id+"F0.wireOp",EDGE,"E12.filletArc"),sQuery(id+"F0.wireOp",EDGE,"E22.MirrorCS"),sQuery(id+"F0.wireOp",EDGE,"E13.filletArc"),sQuery(id+"F0.wireOp",EDGE,"E1"),sQuery(id+"F0.wireOp",EDGE,"E27.MirrorCS"),sQuery(id+"F0.wireOp",EDGE,"E35.MirrorCS"),sQuery(id+"F0.wireOp",EDGE,"E37.MirrorCS"),sQuery(id+"F0.wireOp",EDGE,"E42.MirrorCS"),sQuery(id+"F0.wireOp",EDGE,"E38.MirrorCS"),sQuery(id+"F0.wireOp",EDGE,"E45.MirrorCS"),sQuery(id+"F0.wireOp",EDGE,"E39.MirrorCS"),sQuery(id+"F0.wireOp",EDGE,"E36.MirrorCS"),sQuery(id+"F0.wireOp",EDGE,"E41.MirrorCS"),sQuery(id+"F0.wireOp",EDGE,"E47.MirrorCS"),sQuery(id+"F0.wireOp",EDGE,"E44.MirrorCS"),sQuery(id+"F0.wireOp",EDGE,"E43.MirrorCS"),sQuery(id+"F0.wireOp",EDGE,"E40.MirrorCS"),sQuery(id+"F0.wireOp",EDGE,"E49.MirrorCS"),sQuery(id+"F0.wireOp",EDGE,"E48.MirrorCS"),sQuery(id+"F0.wireOp",EDGE,"E50.MirrorCS"),sQuery(id+"F0.wireOp",EDGE,"E51.MirrorCS"),sQuery(id+"F0.wireOp",EDGE,"E53.MirrorCS"),sQuery(id+"F0.wireOp",EDGE,"E57.MirrorCS"),sQuery(id+"F0.wireOp",EDGE,"E60.MirrorCS"),sQuery(id+"F0.wireOp",EDGE,"E63.MirrorCS"),sQuery(id+"F0.wireOp",EDGE,"E59.MirrorCS"),sQuery(id+"F0.wireOp",EDGE,"E58.MirrorCS"),sQuery(id+"F0.wireOp",EDGE,"E69.0.1.43"),sQuery(id+"F0.wireOp",EDGE,"E69.0.1.59"),sQuery(id+"F0.wireOp",EDGE,"E69.0.1.60"),sQuery(id+"F0.wireOp",EDGE,"E69.0.1.68"),sQuery(id+"F0.wireOp",EDGE,"E69.0.1.89"),sQuery(id+"F0.wireOp",EDGE,"E69.0.1.92"),sQuery(id+"F0.wireOp",EDGE,"E69.0.1.93"),sQuery(id+"F0.wireOp",EDGE,"E69.0.1.94"),sQuery(id+"F0.wireOp",EDGE,"E69.0.1.95"),sQuery(id+"F0.wireOp",EDGE,"E69.0.1.96"),sQuery(id+"F0.wireOp",EDGE,"E69.0.1.105"),sQuery(id+"F0.wireOp",EDGE,"E69.0.1.112"),sQuery(id+"F0.wireOp",EDGE,"E69.0.1.113"),sQuery(id+"F0.wireOp",EDGE,"E69.0.1.119"),sQuery(id+"F0.wireOp",EDGE,"E69.0.1.121"),sQuery(id+"F0.wireOp",EDGE,"E69.0.1.123"),sQuery(id+"F0.wireOp",EDGE,"E69.0.1.127"),sQuery(id+"F0.wireOp",EDGE,"E69.0.1.128"),sQuery(id+"F0.wireOp",EDGE,"E69.0.1.129"),sQuery(id+"F0.wireOp",EDGE,"E69.0.1.133"),sQuery(id+"F0.wireOp",EDGE,"E69.0.1.134"),sQuery(id+"F0.wireOp",EDGE,"E69.0.1.140"),sQuery(id+"F0.wireOp",EDGE,"E69.0.1.141"),sQuery(id+"F0.wireOp",EDGE,"E69.0.1.142"),sQuery(id+"F0.wireOp",EDGE,"E69.0.2.41"),sQuery(id+"F0.wireOp",EDGE,"E69.0.2.43"),sQuery(id+"F0.wireOp",EDGE,"E69.0.2.44"),sQuery(id+"F0.wireOp",EDGE,"E69.0.2.55"),sQuery(id+"F0.wireOp",EDGE,"E69.0.2.59"),sQuery(id+"F0.wireOp",EDGE,"E69.0.2.60"),sQuery(id+"F0.wireOp",EDGE,"E69.0.2.61"),sQuery(id+"F0.wireOp",EDGE,"E69.0.2.68"),sQuery(id+"F0.wireOp",EDGE,"E69.0.2.69"),sQuery(id+"F0.wireOp",EDGE,"E69.0.2.75"),sQuery(id+"F0.wireOp",EDGE,"E69.0.2.84"),sQuery(id+"F0.wireOp",EDGE,"E69.0.2.88"),sQuery(id+"F0.wireOp",EDGE,"E69.0.2.89"),sQuery(id+"F0.wireOp",EDGE,"E69.0.2.92"),sQuery(id+"F0.wireOp",EDGE,"E69.0.2.93"),sQuery(id+"F0.wireOp",EDGE,"E69.0.2.94"),sQuery(id+"F0.wireOp",EDGE,"E69.0.2.95"),sQuery(id+"F0.wireOp",EDGE,"E69.0.2.96"),sQuery(id+"F0.wireOp",EDGE,"E69.0.2.105"),sQuery(id+"F0.wireOp",EDGE,"E69.0.2.112"),sQuery(id+"F0.wireOp",EDGE,"E69.0.2.113"),sQuery(id+"F0.wireOp",EDGE,"E69.0.2.119"),sQuery(id+"F0.wireOp",EDGE,"E69.0.2.121"),sQuery(id+"F0.wireOp",EDGE,"E69.0.2.123"),sQuery(id+"F0.wireOp",EDGE,"E69.0.2.127"),sQuery(id+"F0.wireOp",EDGE,"E69.0.2.128"),sQuery(id+"F0.wireOp",EDGE,"E69.0.2.129"),sQuery(id+"F0.wireOp",EDGE,"E69.0.2.133"),sQuery(id+"F0.wireOp",EDGE,"E69.0.2.134"),sQuery(id+"F0.wireOp",EDGE,"E69.0.2.135"),sQuery(id+"F0.wireOp",EDGE,"E69.0.2.136"),sQuery(id+"F0.wireOp",EDGE,"E69.0.2.140"),sQuery(id+"F0.wireOp",EDGE,"E69.0.2.141"),sQuery(id+"F0.wireOp",EDGE,"E69.0.2.142"),sQuery(id+"F0.wireOp",EDGE,"E70.bottom"),sQuery(id+"F0.wireOp",EDGE,"E70.top"),sQuery(id+"F0.wireOp",EDGE,"E70.left"),sQuery(id+"F0.wireOp",EDGE,"E70.right")])]});
            var Q1;
            Q1=makeQuery(id+"F1.opExtrude","SWEPT_BODY",BODY,{"disambiguationData":[OSD([sQuery(id+"F0.wireOp",EDGE,"E69.0.1.55"),sQuery(id+"F0.wireOp",EDGE,"E69.0.1.61"),sQuery(id+"F0.wireOp",EDGE,"E69.0.1.69"),sQuery(id+"F0.wireOp",EDGE,"E69.0.1.84"),sQuery(id+"F0.wireOp",EDGE,"E69.0.1.135"),sQuery(id+"F0.wireOp",EDGE,"E69.0.2.18"),sQuery(id+"F0.wireOp",EDGE,"E69.0.2.45"),sQuery(id+"F0.wireOp",EDGE,"E69.0.2.62"),sQuery(id+"F0.wireOp",EDGE,"E69.0.2.65"),sQuery(id+"F0.wireOp",EDGE,"E69.0.2.117"),sQuery(id+"F0.wireOp",EDGE,"E69.0.2.126")])]});
            var Q2;
            Q2=makeQuery(id+"F1.opExtrude","SWEPT_BODY",BODY,{"disambiguationData":[OSD([sQuery(id+"F0.wireOp",EDGE,"E69.0.1.41"),sQuery(id+"F0.wireOp",EDGE,"E69.0.1.44"),sQuery(id+"F0.wireOp",EDGE,"E69.0.1.75"),sQuery(id+"F0.wireOp",EDGE,"E69.0.1.88"),sQuery(id+"F0.wireOp",EDGE,"E69.0.1.136"),sQuery(id+"F0.wireOp",EDGE,"E69.0.2.17"),sQuery(id+"F0.wireOp",EDGE,"E69.0.2.48"),sQuery(id+"F0.wireOp",EDGE,"E69.0.2.50"),sQuery(id+"F0.wireOp",EDGE,"E69.0.2.57"),sQuery(id+"F0.wireOp",EDGE,"E69.0.2.118"),sQuery(id+"F0.wireOp",EDGE,"E69.0.2.130")])]});
            var Q3;
            Q3=makeQuery(id+"F1.opExtrude","SWEPT_BODY",BODY,{"disambiguationData":[OSD([sQuery(id+"F0.wireOp",EDGE,"E15.filletArc"),sQuery(id+"F0.wireOp",EDGE,"E11"),sQuery(id+"F0.wireOp",EDGE,"E10.filletArc"),sQuery(id+"F0.wireOp",EDGE,"E6"),sQuery(id+"F0.wireOp",EDGE,"E4"),sQuery(id+"F0.wireOp",EDGE,"E69.0.1.17"),sQuery(id+"F0.wireOp",EDGE,"E69.0.1.48"),sQuery(id+"F0.wireOp",EDGE,"E69.0.1.50"),sQuery(id+"F0.wireOp",EDGE,"E69.0.1.57"),sQuery(id+"F0.wireOp",EDGE,"E69.0.1.118"),sQuery(id+"F0.wireOp",EDGE,"E69.0.1.130")])]});
            var Q4;
            Q4=makeQuery(id+"F1.opExtrude","SWEPT_BODY",BODY,{"disambiguationData":[OSD([sQuery(id+"F0.wireOp",EDGE,"E16.MirrorCS"),sQuery(id+"F0.wireOp",EDGE,"E23.MirrorCS"),sQuery(id+"F0.wireOp",EDGE,"E24.MirrorCS"),sQuery(id+"F0.wireOp",EDGE,"E28.MirrorCS"),sQuery(id+"F0.wireOp",EDGE,"E26.MirrorCS"),sQuery(id+"F0.wireOp",EDGE,"E69.0.1.18"),sQuery(id+"F0.wireOp",EDGE,"E69.0.1.45"),sQuery(id+"F0.wireOp",EDGE,"E69.0.1.62"),sQuery(id+"F0.wireOp",EDGE,"E69.0.1.65"),sQuery(id+"F0.wireOp",EDGE,"E69.0.1.117"),sQuery(id+"F0.wireOp",EDGE,"E69.0.1.126")])]});
            var Q5;
            Q5=qCreatedBy(makeId("Front.planeOp"),FACE);
            transform(context, id + "F2", {"entities" : qUnion([Q0, Q1, Q2, Q3, Q4]), "transformType" : TransformType.TRANSLATION_DISTANCE, "transformDirection" : qUnion([Q5]), "distance" : 25.4 * mm, "oppositeDirection" : true, "makeCopy" : false});
        }
        {
            var Q0;
            Q0=makeQuery(id+"F1.opExtrude","CAP_FACE",FACE,{"disambiguationData":[OSD([sQuery(id+"F0.wireOp",EDGE,"E5"),sQuery(id+"F0.wireOp",EDGE,"E8.MirrorCS"),sQuery(id+"F0.wireOp",EDGE,"E17.MirrorCS"),sQuery(id+"F0.wireOp",EDGE,"E18.MirrorCS"),sQuery(id+"F0.wireOp",EDGE,"E14.filletArc"),sQuery(id+"F0.wireOp",EDGE,"E20.MirrorCS"),sQuery(id+"F0.wireOp",EDGE,"E19.MirrorCS"),sQuery(id+"F0.wireOp",EDGE,"E3"),sQuery(id+"F0.wireOp",EDGE,"E2.left"),sQuery(id+"F0.wireOp",EDGE,"E12.filletArc"),sQuery(id+"F0.wireOp",EDGE,"E22.MirrorCS"),sQuery(id+"F0.wireOp",EDGE,"E13.filletArc"),sQuery(id+"F0.wireOp",EDGE,"E1"),sQuery(id+"F0.wireOp",EDGE,"E27.MirrorCS"),sQuery(id+"F0.wireOp",EDGE,"E35.MirrorCS"),sQuery(id+"F0.wireOp",EDGE,"E37.MirrorCS"),sQuery(id+"F0.wireOp",EDGE,"E42.MirrorCS"),sQuery(id+"F0.wireOp",EDGE,"E38.MirrorCS"),sQuery(id+"F0.wireOp",EDGE,"E45.MirrorCS"),sQuery(id+"F0.wireOp",EDGE,"E39.MirrorCS"),sQuery(id+"F0.wireOp",EDGE,"E36.MirrorCS"),sQuery(id+"F0.wireOp",EDGE,"E41.MirrorCS"),sQuery(id+"F0.wireOp",EDGE,"E47.MirrorCS"),sQuery(id+"F0.wireOp",EDGE,"E44.MirrorCS"),sQuery(id+"F0.wireOp",EDGE,"E43.MirrorCS"),sQuery(id+"F0.wireOp",EDGE,"E40.MirrorCS"),sQuery(id+"F0.wireOp",EDGE,"E49.MirrorCS"),sQuery(id+"F0.wireOp",EDGE,"E48.MirrorCS"),sQuery(id+"F0.wireOp",EDGE,"E50.MirrorCS"),sQuery(id+"F0.wireOp",EDGE,"E51.MirrorCS"),sQuery(id+"F0.wireOp",EDGE,"E53.MirrorCS"),sQuery(id+"F0.wireOp",EDGE,"E57.MirrorCS"),sQuery(id+"F0.wireOp",EDGE,"E60.MirrorCS"),sQuery(id+"F0.wireOp",EDGE,"E63.MirrorCS"),sQuery(id+"F0.wireOp",EDGE,"E59.MirrorCS"),sQuery(id+"F0.wireOp",EDGE,"E58.MirrorCS"),sQuery(id+"F0.wireOp",EDGE,"E69.0.1.43"),sQuery(id+"F0.wireOp",EDGE,"E69.0.1.59"),sQuery(id+"F0.wireOp",EDGE,"E69.0.1.60"),sQuery(id+"F0.wireOp",EDGE,"E69.0.1.68"),sQuery(id+"F0.wireOp",EDGE,"E69.0.1.89"),sQuery(id+"F0.wireOp",EDGE,"E69.0.1.92"),sQuery(id+"F0.wireOp",EDGE,"E69.0.1.93"),sQuery(id+"F0.wireOp",EDGE,"E69.0.1.94"),sQuery(id+"F0.wireOp",EDGE,"E69.0.1.95"),sQuery(id+"F0.wireOp",EDGE,"E69.0.1.96"),sQuery(id+"F0.wireOp",EDGE,"E69.0.1.105"),sQuery(id+"F0.wireOp",EDGE,"E69.0.1.112"),sQuery(id+"F0.wireOp",EDGE,"E69.0.1.113"),sQuery(id+"F0.wireOp",EDGE,"E69.0.1.119"),sQuery(id+"F0.wireOp",EDGE,"E69.0.1.121"),sQuery(id+"F0.wireOp",EDGE,"E69.0.1.123"),sQuery(id+"F0.wireOp",EDGE,"E69.0.1.127"),sQuery(id+"F0.wireOp",EDGE,"E69.0.1.128"),sQuery(id+"F0.wireOp",EDGE,"E69.0.1.129"),sQuery(id+"F0.wireOp",EDGE,"E69.0.1.133"),sQuery(id+"F0.wireOp",EDGE,"E69.0.1.134"),sQuery(id+"F0.wireOp",EDGE,"E69.0.1.140"),sQuery(id+"F0.wireOp",EDGE,"E69.0.1.141"),sQuery(id+"F0.wireOp",EDGE,"E69.0.1.142"),sQuery(id+"F0.wireOp",EDGE,"E69.0.2.41"),sQuery(id+"F0.wireOp",EDGE,"E69.0.2.43"),sQuery(id+"F0.wireOp",EDGE,"E69.0.2.44"),sQuery(id+"F0.wireOp",EDGE,"E69.0.2.55"),sQuery(id+"F0.wireOp",EDGE,"E69.0.2.59"),sQuery(id+"F0.wireOp",EDGE,"E69.0.2.60"),sQuery(id+"F0.wireOp",EDGE,"E69.0.2.61"),sQuery(id+"F0.wireOp",EDGE,"E69.0.2.68"),sQuery(id+"F0.wireOp",EDGE,"E69.0.2.69"),sQuery(id+"F0.wireOp",EDGE,"E69.0.2.75"),sQuery(id+"F0.wireOp",EDGE,"E69.0.2.84"),sQuery(id+"F0.wireOp",EDGE,"E69.0.2.88"),sQuery(id+"F0.wireOp",EDGE,"E69.0.2.89"),sQuery(id+"F0.wireOp",EDGE,"E69.0.2.92"),sQuery(id+"F0.wireOp",EDGE,"E69.0.2.93"),sQuery(id+"F0.wireOp",EDGE,"E69.0.2.94"),sQuery(id+"F0.wireOp",EDGE,"E69.0.2.95"),sQuery(id+"F0.wireOp",EDGE,"E69.0.2.96"),sQuery(id+"F0.wireOp",EDGE,"E69.0.2.105"),sQuery(id+"F0.wireOp",EDGE,"E69.0.2.112"),sQuery(id+"F0.wireOp",EDGE,"E69.0.2.113"),sQuery(id+"F0.wireOp",EDGE,"E69.0.2.119"),sQuery(id+"F0.wireOp",EDGE,"E69.0.2.121"),sQuery(id+"F0.wireOp",EDGE,"E69.0.2.123"),sQuery(id+"F0.wireOp",EDGE,"E69.0.2.127"),sQuery(id+"F0.wireOp",EDGE,"E69.0.2.128"),sQuery(id+"F0.wireOp",EDGE,"E69.0.2.129"),sQuery(id+"F0.wireOp",EDGE,"E69.0.2.133"),sQuery(id+"F0.wireOp",EDGE,"E69.0.2.134"),sQuery(id+"F0.wireOp",EDGE,"E69.0.2.135"),sQuery(id+"F0.wireOp",EDGE,"E69.0.2.136"),sQuery(id+"F0.wireOp",EDGE,"E69.0.2.140"),sQuery(id+"F0.wireOp",EDGE,"E69.0.2.141"),sQuery(id+"F0.wireOp",EDGE,"E69.0.2.142"),sQuery(id+"F0.wireOp",EDGE,"E70.bottom"),sQuery(id+"F0.wireOp",EDGE,"E70.top"),sQuery(id+"F0.wireOp",EDGE,"E70.left"),sQuery(id+"F0.wireOp",EDGE,"E70.right")])],"isStart":true});
            var sketch = newSketch(context, id + "F3", { "sketchPlane" : qUnion([Q0])});
            skLineSegment(sketch, "E71.bottom", {"start": v(-20.32, 35.13) * mm, "end": v(20.32, 35.13) * mm});
            skLineSegment(sketch, "E71.top", {"start": v(-20.32, -8.98) * mm, "end": v(20.32, -8.98) * mm});
            skLineSegment(sketch, "E71.left", {"start": v(-20.32, 35.13) * mm, "end": v(-20.32, -8.98) * mm});
            skLineSegment(sketch, "E71.right", {"start": v(20.32, 35.13) * mm, "end": v(20.32, -8.98) * mm});
            skSolve(sketch);
        }
        {
            var Q0;
            Q0=qSketchRegion(id+"F3",true);
            extrude(context, id + "F4", {"entities" : qUnion([Q0]), "operationType" : NewBodyOperationType.ADD, "depth" : 12.7 * mm, "offsetDistance" : 25.4 * mm});
        }
        {
            var Q0;
            Q0=makeQuery(id+"F4.opExtrude","CAP_EDGE",EDGE,{"disambiguationData":[OSD([sQuery(id+"F3.wireOp",EDGE,"E71.left")])],"isStart":false});
            cPoint(context, id + "F5", {"entities" : qUnion([Q0]), "parameter" : 0.5});
        }
        {
            var Q0;
            Q0=makeQuery(id+"F1.opExtrude","SWEPT_BODY",BODY,{"disambiguationData":[OSD([sQuery(id+"F0.wireOp",EDGE,"E5"),sQuery(id+"F0.wireOp",EDGE,"E8.MirrorCS"),sQuery(id+"F0.wireOp",EDGE,"E17.MirrorCS"),sQuery(id+"F0.wireOp",EDGE,"E18.MirrorCS"),sQuery(id+"F0.wireOp",EDGE,"E14.filletArc"),sQuery(id+"F0.wireOp",EDGE,"E20.MirrorCS"),sQuery(id+"F0.wireOp",EDGE,"E19.MirrorCS"),sQuery(id+"F0.wireOp",EDGE,"E3"),sQuery(id+"F0.wireOp",EDGE,"E2.left"),sQuery(id+"F0.wireOp",EDGE,"E12.filletArc"),sQuery(id+"F0.wireOp",EDGE,"E22.MirrorCS"),sQuery(id+"F0.wireOp",EDGE,"E13.filletArc"),sQuery(id+"F0.wireOp",EDGE,"E1"),sQuery(id+"F0.wireOp",EDGE,"E27.MirrorCS"),sQuery(id+"F0.wireOp",EDGE,"E35.MirrorCS"),sQuery(id+"F0.wireOp",EDGE,"E37.MirrorCS"),sQuery(id+"F0.wireOp",EDGE,"E42.MirrorCS"),sQuery(id+"F0.wireOp",EDGE,"E38.MirrorCS"),sQuery(id+"F0.wireOp",EDGE,"E45.MirrorCS"),sQuery(id+"F0.wireOp",EDGE,"E39.MirrorCS"),sQuery(id+"F0.wireOp",EDGE,"E36.MirrorCS"),sQuery(id+"F0.wireOp",EDGE,"E41.MirrorCS"),sQuery(id+"F0.wireOp",EDGE,"E47.MirrorCS"),sQuery(id+"F0.wireOp",EDGE,"E44.MirrorCS"),sQuery(id+"F0.wireOp",EDGE,"E43.MirrorCS"),sQuery(id+"F0.wireOp",EDGE,"E40.MirrorCS"),sQuery(id+"F0.wireOp",EDGE,"E49.MirrorCS"),sQuery(id+"F0.wireOp",EDGE,"E48.MirrorCS"),sQuery(id+"F0.wireOp",EDGE,"E50.MirrorCS"),sQuery(id+"F0.wireOp",EDGE,"E51.MirrorCS"),sQuery(id+"F0.wireOp",EDGE,"E53.MirrorCS"),sQuery(id+"F0.wireOp",EDGE,"E57.MirrorCS"),sQuery(id+"F0.wireOp",EDGE,"E60.MirrorCS"),sQuery(id+"F0.wireOp",EDGE,"E63.MirrorCS"),sQuery(id+"F0.wireOp",EDGE,"E59.MirrorCS"),sQuery(id+"F0.wireOp",EDGE,"E58.MirrorCS"),sQuery(id+"F0.wireOp",EDGE,"E69.0.1.43"),sQuery(id+"F0.wireOp",EDGE,"E69.0.1.59"),sQuery(id+"F0.wireOp",EDGE,"E69.0.1.60"),sQuery(id+"F0.wireOp",EDGE,"E69.0.1.68"),sQuery(id+"F0.wireOp",EDGE,"E69.0.1.89"),sQuery(id+"F0.wireOp",EDGE,"E69.0.1.92"),sQuery(id+"F0.wireOp",EDGE,"E69.0.1.93"),sQuery(id+"F0.wireOp",EDGE,"E69.0.1.94"),sQuery(id+"F0.wireOp",EDGE,"E69.0.1.95"),sQuery(id+"F0.wireOp",EDGE,"E69.0.1.96"),sQuery(id+"F0.wireOp",EDGE,"E69.0.1.105"),sQuery(id+"F0.wireOp",EDGE,"E69.0.1.112"),sQuery(id+"F0.wireOp",EDGE,"E69.0.1.113"),sQuery(id+"F0.wireOp",EDGE,"E69.0.1.119"),sQuery(id+"F0.wireOp",EDGE,"E69.0.1.121"),sQuery(id+"F0.wireOp",EDGE,"E69.0.1.123"),sQuery(id+"F0.wireOp",EDGE,"E69.0.1.127"),sQuery(id+"F0.wireOp",EDGE,"E69.0.1.128"),sQuery(id+"F0.wireOp",EDGE,"E69.0.1.129"),sQuery(id+"F0.wireOp",EDGE,"E69.0.1.133"),sQuery(id+"F0.wireOp",EDGE,"E69.0.1.134"),sQuery(id+"F0.wireOp",EDGE,"E69.0.1.140"),sQuery(id+"F0.wireOp",EDGE,"E69.0.1.141"),sQuery(id+"F0.wireOp",EDGE,"E69.0.1.142"),sQuery(id+"F0.wireOp",EDGE,"E69.0.2.41"),sQuery(id+"F0.wireOp",EDGE,"E69.0.2.43"),sQuery(id+"F0.wireOp",EDGE,"E69.0.2.44"),sQuery(id+"F0.wireOp",EDGE,"E69.0.2.55"),sQuery(id+"F0.wireOp",EDGE,"E69.0.2.59"),sQuery(id+"F0.wireOp",EDGE,"E69.0.2.60"),sQuery(id+"F0.wireOp",EDGE,"E69.0.2.61"),sQuery(id+"F0.wireOp",EDGE,"E69.0.2.68"),sQuery(id+"F0.wireOp",EDGE,"E69.0.2.69"),sQuery(id+"F0.wireOp",EDGE,"E69.0.2.75"),sQuery(id+"F0.wireOp",EDGE,"E69.0.2.84"),sQuery(id+"F0.wireOp",EDGE,"E69.0.2.88"),sQuery(id+"F0.wireOp",EDGE,"E69.0.2.89"),sQuery(id+"F0.wireOp",EDGE,"E69.0.2.92"),sQuery(id+"F0.wireOp",EDGE,"E69.0.2.93"),sQuery(id+"F0.wireOp",EDGE,"E69.0.2.94"),sQuery(id+"F0.wireOp",EDGE,"E69.0.2.95"),sQuery(id+"F0.wireOp",EDGE,"E69.0.2.96"),sQuery(id+"F0.wireOp",EDGE,"E69.0.2.105"),sQuery(id+"F0.wireOp",EDGE,"E69.0.2.112"),sQuery(id+"F0.wireOp",EDGE,"E69.0.2.113"),sQuery(id+"F0.wireOp",EDGE,"E69.0.2.119"),sQuery(id+"F0.wireOp",EDGE,"E69.0.2.121"),sQuery(id+"F0.wireOp",EDGE,"E69.0.2.123"),sQuery(id+"F0.wireOp",EDGE,"E69.0.2.127"),sQuery(id+"F0.wireOp",EDGE,"E69.0.2.128"),sQuery(id+"F0.wireOp",EDGE,"E69.0.2.129"),sQuery(id+"F0.wireOp",EDGE,"E69.0.2.133"),sQuery(id+"F0.wireOp",EDGE,"E69.0.2.134"),sQuery(id+"F0.wireOp",EDGE,"E69.0.2.135"),sQuery(id+"F0.wireOp",EDGE,"E69.0.2.136"),sQuery(id+"F0.wireOp",EDGE,"E69.0.2.140"),sQuery(id+"F0.wireOp",EDGE,"E69.0.2.141"),sQuery(id+"F0.wireOp",EDGE,"E69.0.2.142"),sQuery(id+"F0.wireOp",EDGE,"E70.bottom"),sQuery(id+"F0.wireOp",EDGE,"E70.top"),sQuery(id+"F0.wireOp",EDGE,"E70.left"),sQuery(id+"F0.wireOp",EDGE,"E70.right")])]});
            var Q1;
            Q1=qCreatedBy(id+"F5",VERTEX);
            var Q2;
            Q2=qCreatedBy(makeId("Origin.pointOp"),VERTEX);
            transform(context, id + "F6", {"entities" : qUnion([Q0]), "transformType" : TransformType.TRANSLATION_ENTITY, "oppositeDirectionEntity" : false, "transformLine" : qUnion([Q1, Q2]), "makeCopy" : false});
        }
        {
            var Q0;
            Q0=makeQuery(id+"F1.opExtrude","SWEPT_BODY",BODY,{"disambiguationData":[OSD([sQuery(id+"F0.wireOp",EDGE,"E5"),sQuery(id+"F0.wireOp",EDGE,"E8.MirrorCS"),sQuery(id+"F0.wireOp",EDGE,"E17.MirrorCS"),sQuery(id+"F0.wireOp",EDGE,"E18.MirrorCS"),sQuery(id+"F0.wireOp",EDGE,"E14.filletArc"),sQuery(id+"F0.wireOp",EDGE,"E20.MirrorCS"),sQuery(id+"F0.wireOp",EDGE,"E19.MirrorCS"),sQuery(id+"F0.wireOp",EDGE,"E3"),sQuery(id+"F0.wireOp",EDGE,"E2.left"),sQuery(id+"F0.wireOp",EDGE,"E12.filletArc"),sQuery(id+"F0.wireOp",EDGE,"E22.MirrorCS"),sQuery(id+"F0.wireOp",EDGE,"E13.filletArc"),sQuery(id+"F0.wireOp",EDGE,"E1"),sQuery(id+"F0.wireOp",EDGE,"E27.MirrorCS"),sQuery(id+"F0.wireOp",EDGE,"E35.MirrorCS"),sQuery(id+"F0.wireOp",EDGE,"E37.MirrorCS"),sQuery(id+"F0.wireOp",EDGE,"E42.MirrorCS"),sQuery(id+"F0.wireOp",EDGE,"E38.MirrorCS"),sQuery(id+"F0.wireOp",EDGE,"E45.MirrorCS"),sQuery(id+"F0.wireOp",EDGE,"E39.MirrorCS"),sQuery(id+"F0.wireOp",EDGE,"E36.MirrorCS"),sQuery(id+"F0.wireOp",EDGE,"E41.MirrorCS"),sQuery(id+"F0.wireOp",EDGE,"E47.MirrorCS"),sQuery(id+"F0.wireOp",EDGE,"E44.MirrorCS"),sQuery(id+"F0.wireOp",EDGE,"E43.MirrorCS"),sQuery(id+"F0.wireOp",EDGE,"E40.MirrorCS"),sQuery(id+"F0.wireOp",EDGE,"E49.MirrorCS"),sQuery(id+"F0.wireOp",EDGE,"E48.MirrorCS"),sQuery(id+"F0.wireOp",EDGE,"E50.MirrorCS"),sQuery(id+"F0.wireOp",EDGE,"E51.MirrorCS"),sQuery(id+"F0.wireOp",EDGE,"E53.MirrorCS"),sQuery(id+"F0.wireOp",EDGE,"E57.MirrorCS"),sQuery(id+"F0.wireOp",EDGE,"E60.MirrorCS"),sQuery(id+"F0.wireOp",EDGE,"E63.MirrorCS"),sQuery(id+"F0.wireOp",EDGE,"E59.MirrorCS"),sQuery(id+"F0.wireOp",EDGE,"E58.MirrorCS"),sQuery(id+"F0.wireOp",EDGE,"E69.0.1.43"),sQuery(id+"F0.wireOp",EDGE,"E69.0.1.59"),sQuery(id+"F0.wireOp",EDGE,"E69.0.1.60"),sQuery(id+"F0.wireOp",EDGE,"E69.0.1.68"),sQuery(id+"F0.wireOp",EDGE,"E69.0.1.89"),sQuery(id+"F0.wireOp",EDGE,"E69.0.1.92"),sQuery(id+"F0.wireOp",EDGE,"E69.0.1.93"),sQuery(id+"F0.wireOp",EDGE,"E69.0.1.94"),sQuery(id+"F0.wireOp",EDGE,"E69.0.1.95"),sQuery(id+"F0.wireOp",EDGE,"E69.0.1.96"),sQuery(id+"F0.wireOp",EDGE,"E69.0.1.105"),sQuery(id+"F0.wireOp",EDGE,"E69.0.1.112"),sQuery(id+"F0.wireOp",EDGE,"E69.0.1.113"),sQuery(id+"F0.wireOp",EDGE,"E69.0.1.119"),sQuery(id+"F0.wireOp",EDGE,"E69.0.1.121"),sQuery(id+"F0.wireOp",EDGE,"E69.0.1.123"),sQuery(id+"F0.wireOp",EDGE,"E69.0.1.127"),sQuery(id+"F0.wireOp",EDGE,"E69.0.1.128"),sQuery(id+"F0.wireOp",EDGE,"E69.0.1.129"),sQuery(id+"F0.wireOp",EDGE,"E69.0.1.133"),sQuery(id+"F0.wireOp",EDGE,"E69.0.1.134"),sQuery(id+"F0.wireOp",EDGE,"E69.0.1.140"),sQuery(id+"F0.wireOp",EDGE,"E69.0.1.141"),sQuery(id+"F0.wireOp",EDGE,"E69.0.1.142"),sQuery(id+"F0.wireOp",EDGE,"E69.0.2.41"),sQuery(id+"F0.wireOp",EDGE,"E69.0.2.43"),sQuery(id+"F0.wireOp",EDGE,"E69.0.2.44"),sQuery(id+"F0.wireOp",EDGE,"E69.0.2.55"),sQuery(id+"F0.wireOp",EDGE,"E69.0.2.59"),sQuery(id+"F0.wireOp",EDGE,"E69.0.2.60"),sQuery(id+"F0.wireOp",EDGE,"E69.0.2.61"),sQuery(id+"F0.wireOp",EDGE,"E69.0.2.68"),sQuery(id+"F0.wireOp",EDGE,"E69.0.2.69"),sQuery(id+"F0.wireOp",EDGE,"E69.0.2.75"),sQuery(id+"F0.wireOp",EDGE,"E69.0.2.84"),sQuery(id+"F0.wireOp",EDGE,"E69.0.2.88"),sQuery(id+"F0.wireOp",EDGE,"E69.0.2.89"),sQuery(id+"F0.wireOp",EDGE,"E69.0.2.92"),sQuery(id+"F0.wireOp",EDGE,"E69.0.2.93"),sQuery(id+"F0.wireOp",EDGE,"E69.0.2.94"),sQuery(id+"F0.wireOp",EDGE,"E69.0.2.95"),sQuery(id+"F0.wireOp",EDGE,"E69.0.2.96"),sQuery(id+"F0.wireOp",EDGE,"E69.0.2.105"),sQuery(id+"F0.wireOp",EDGE,"E69.0.2.112"),sQuery(id+"F0.wireOp",EDGE,"E69.0.2.113"),sQuery(id+"F0.wireOp",EDGE,"E69.0.2.119"),sQuery(id+"F0.wireOp",EDGE,"E69.0.2.121"),sQuery(id+"F0.wireOp",EDGE,"E69.0.2.123"),sQuery(id+"F0.wireOp",EDGE,"E69.0.2.127"),sQuery(id+"F0.wireOp",EDGE,"E69.0.2.128"),sQuery(id+"F0.wireOp",EDGE,"E69.0.2.129"),sQuery(id+"F0.wireOp",EDGE,"E69.0.2.133"),sQuery(id+"F0.wireOp",EDGE,"E69.0.2.134"),sQuery(id+"F0.wireOp",EDGE,"E69.0.2.135"),sQuery(id+"F0.wireOp",EDGE,"E69.0.2.136"),sQuery(id+"F0.wireOp",EDGE,"E69.0.2.140"),sQuery(id+"F0.wireOp",EDGE,"E69.0.2.141"),sQuery(id+"F0.wireOp",EDGE,"E69.0.2.142"),sQuery(id+"F0.wireOp",EDGE,"E70.bottom"),sQuery(id+"F0.wireOp",EDGE,"E70.top"),sQuery(id+"F0.wireOp",EDGE,"E70.left"),sQuery(id+"F0.wireOp",EDGE,"E70.right")])]});
            var Q1;
            Q1=qCreatedBy(makeId("Front.planeOp"),FACE);
            transform(context, id + "F7", {"entities" : qUnion([Q0]), "transformType" : TransformType.TRANSLATION_DISTANCE, "transformDirection" : qUnion([Q1]), "distance" : 38.1 * mm, "oppositeDirection" : true, "makeCopy" : false});
        }
        {
            var Q0;
            Q0=qCreatedBy(makeId("Top.planeOp"),FACE);
            var sketch = newSketch(context, id + "F8", { "sketchPlane" : qUnion([Q0])});
            skLineSegment(sketch, "E72", {"start": v(0, 0) * mm, "end": v(119.14, 0) * mm});
            skLineSegment(sketch, "E73", {"start": v(0, 0) * mm, "end": v(-87.16, 0) * mm});
            skLineSegment(sketch, "E74", {"start": v(-87.16, 0) * mm, "end": v(119.14, 0) * mm});
            skSolve(sketch);
        }
        {
            var Q0;
            Q0=makeQuery(id+"F1.opExtrude","SWEPT_BODY",BODY,{"disambiguationData":[OSD([sQuery(id+"F0.wireOp",EDGE,"E5"),sQuery(id+"F0.wireOp",EDGE,"E8.MirrorCS"),sQuery(id+"F0.wireOp",EDGE,"E17.MirrorCS"),sQuery(id+"F0.wireOp",EDGE,"E18.MirrorCS"),sQuery(id+"F0.wireOp",EDGE,"E14.filletArc"),sQuery(id+"F0.wireOp",EDGE,"E20.MirrorCS"),sQuery(id+"F0.wireOp",EDGE,"E19.MirrorCS"),sQuery(id+"F0.wireOp",EDGE,"E3"),sQuery(id+"F0.wireOp",EDGE,"E2.left"),sQuery(id+"F0.wireOp",EDGE,"E12.filletArc"),sQuery(id+"F0.wireOp",EDGE,"E22.MirrorCS"),sQuery(id+"F0.wireOp",EDGE,"E13.filletArc"),sQuery(id+"F0.wireOp",EDGE,"E1"),sQuery(id+"F0.wireOp",EDGE,"E27.MirrorCS"),sQuery(id+"F0.wireOp",EDGE,"E35.MirrorCS"),sQuery(id+"F0.wireOp",EDGE,"E37.MirrorCS"),sQuery(id+"F0.wireOp",EDGE,"E42.MirrorCS"),sQuery(id+"F0.wireOp",EDGE,"E38.MirrorCS"),sQuery(id+"F0.wireOp",EDGE,"E45.MirrorCS"),sQuery(id+"F0.wireOp",EDGE,"E39.MirrorCS"),sQuery(id+"F0.wireOp",EDGE,"E36.MirrorCS"),sQuery(id+"F0.wireOp",EDGE,"E41.MirrorCS"),sQuery(id+"F0.wireOp",EDGE,"E47.MirrorCS"),sQuery(id+"F0.wireOp",EDGE,"E44.MirrorCS"),sQuery(id+"F0.wireOp",EDGE,"E43.MirrorCS"),sQuery(id+"F0.wireOp",EDGE,"E40.MirrorCS"),sQuery(id+"F0.wireOp",EDGE,"E49.MirrorCS"),sQuery(id+"F0.wireOp",EDGE,"E48.MirrorCS"),sQuery(id+"F0.wireOp",EDGE,"E50.MirrorCS"),sQuery(id+"F0.wireOp",EDGE,"E51.MirrorCS"),sQuery(id+"F0.wireOp",EDGE,"E53.MirrorCS"),sQuery(id+"F0.wireOp",EDGE,"E57.MirrorCS"),sQuery(id+"F0.wireOp",EDGE,"E60.MirrorCS"),sQuery(id+"F0.wireOp",EDGE,"E63.MirrorCS"),sQuery(id+"F0.wireOp",EDGE,"E59.MirrorCS"),sQuery(id+"F0.wireOp",EDGE,"E58.MirrorCS"),sQuery(id+"F0.wireOp",EDGE,"E69.0.1.43"),sQuery(id+"F0.wireOp",EDGE,"E69.0.1.59"),sQuery(id+"F0.wireOp",EDGE,"E69.0.1.60"),sQuery(id+"F0.wireOp",EDGE,"E69.0.1.68"),sQuery(id+"F0.wireOp",EDGE,"E69.0.1.89"),sQuery(id+"F0.wireOp",EDGE,"E69.0.1.92"),sQuery(id+"F0.wireOp",EDGE,"E69.0.1.93"),sQuery(id+"F0.wireOp",EDGE,"E69.0.1.94"),sQuery(id+"F0.wireOp",EDGE,"E69.0.1.95"),sQuery(id+"F0.wireOp",EDGE,"E69.0.1.96"),sQuery(id+"F0.wireOp",EDGE,"E69.0.1.105"),sQuery(id+"F0.wireOp",EDGE,"E69.0.1.112"),sQuery(id+"F0.wireOp",EDGE,"E69.0.1.113"),sQuery(id+"F0.wireOp",EDGE,"E69.0.1.119"),sQuery(id+"F0.wireOp",EDGE,"E69.0.1.121"),sQuery(id+"F0.wireOp",EDGE,"E69.0.1.123"),sQuery(id+"F0.wireOp",EDGE,"E69.0.1.127"),sQuery(id+"F0.wireOp",EDGE,"E69.0.1.128"),sQuery(id+"F0.wireOp",EDGE,"E69.0.1.129"),sQuery(id+"F0.wireOp",EDGE,"E69.0.1.133"),sQuery(id+"F0.wireOp",EDGE,"E69.0.1.134"),sQuery(id+"F0.wireOp",EDGE,"E69.0.1.140"),sQuery(id+"F0.wireOp",EDGE,"E69.0.1.141"),sQuery(id+"F0.wireOp",EDGE,"E69.0.1.142"),sQuery(id+"F0.wireOp",EDGE,"E69.0.2.41"),sQuery(id+"F0.wireOp",EDGE,"E69.0.2.43"),sQuery(id+"F0.wireOp",EDGE,"E69.0.2.44"),sQuery(id+"F0.wireOp",EDGE,"E69.0.2.55"),sQuery(id+"F0.wireOp",EDGE,"E69.0.2.59"),sQuery(id+"F0.wireOp",EDGE,"E69.0.2.60"),sQuery(id+"F0.wireOp",EDGE,"E69.0.2.61"),sQuery(id+"F0.wireOp",EDGE,"E69.0.2.68"),sQuery(id+"F0.wireOp",EDGE,"E69.0.2.69"),sQuery(id+"F0.wireOp",EDGE,"E69.0.2.75"),sQuery(id+"F0.wireOp",EDGE,"E69.0.2.84"),sQuery(id+"F0.wireOp",EDGE,"E69.0.2.88"),sQuery(id+"F0.wireOp",EDGE,"E69.0.2.89"),sQuery(id+"F0.wireOp",EDGE,"E69.0.2.92"),sQuery(id+"F0.wireOp",EDGE,"E69.0.2.93"),sQuery(id+"F0.wireOp",EDGE,"E69.0.2.94"),sQuery(id+"F0.wireOp",EDGE,"E69.0.2.95"),sQuery(id+"F0.wireOp",EDGE,"E69.0.2.96"),sQuery(id+"F0.wireOp",EDGE,"E69.0.2.105"),sQuery(id+"F0.wireOp",EDGE,"E69.0.2.112"),sQuery(id+"F0.wireOp",EDGE,"E69.0.2.113"),sQuery(id+"F0.wireOp",EDGE,"E69.0.2.119"),sQuery(id+"F0.wireOp",EDGE,"E69.0.2.121"),sQuery(id+"F0.wireOp",EDGE,"E69.0.2.123"),sQuery(id+"F0.wireOp",EDGE,"E69.0.2.127"),sQuery(id+"F0.wireOp",EDGE,"E69.0.2.128"),sQuery(id+"F0.wireOp",EDGE,"E69.0.2.129"),sQuery(id+"F0.wireOp",EDGE,"E69.0.2.133"),sQuery(id+"F0.wireOp",EDGE,"E69.0.2.134"),sQuery(id+"F0.wireOp",EDGE,"E69.0.2.135"),sQuery(id+"F0.wireOp",EDGE,"E69.0.2.136"),sQuery(id+"F0.wireOp",EDGE,"E69.0.2.140"),sQuery(id+"F0.wireOp",EDGE,"E69.0.2.141"),sQuery(id+"F0.wireOp",EDGE,"E69.0.2.142"),sQuery(id+"F0.wireOp",EDGE,"E70.bottom"),sQuery(id+"F0.wireOp",EDGE,"E70.top"),sQuery(id+"F0.wireOp",EDGE,"E70.left"),sQuery(id+"F0.wireOp",EDGE,"E70.right")])]});
            var Q1;
            Q1=sQuery(id+"F8.wireOp",EDGE,"E74");
            transform(context, id + "F9", {"entities" : qUnion([Q0]), "transformType" : TransformType.ROTATION, "transformAxis" : qUnion([Q1]), "angle" : 59 * degree, "oppositeDirection" : true, "makeCopy" : false});
        }
        {
            var Q0;
            Q0=makeQuery(id+"F1.opExtrude","CAP_FACE",FACE,{"disambiguationData":[OSD([sQuery(id+"F0.wireOp",EDGE,"E5"),sQuery(id+"F0.wireOp",EDGE,"E8.MirrorCS"),sQuery(id+"F0.wireOp",EDGE,"E17.MirrorCS"),sQuery(id+"F0.wireOp",EDGE,"E18.MirrorCS"),sQuery(id+"F0.wireOp",EDGE,"E14.filletArc"),sQuery(id+"F0.wireOp",EDGE,"E20.MirrorCS"),sQuery(id+"F0.wireOp",EDGE,"E19.MirrorCS"),sQuery(id+"F0.wireOp",EDGE,"E3"),sQuery(id+"F0.wireOp",EDGE,"E2.left"),sQuery(id+"F0.wireOp",EDGE,"E12.filletArc"),sQuery(id+"F0.wireOp",EDGE,"E22.MirrorCS"),sQuery(id+"F0.wireOp",EDGE,"E13.filletArc"),sQuery(id+"F0.wireOp",EDGE,"E1"),sQuery(id+"F0.wireOp",EDGE,"E27.MirrorCS"),sQuery(id+"F0.wireOp",EDGE,"E35.MirrorCS"),sQuery(id+"F0.wireOp",EDGE,"E37.MirrorCS"),sQuery(id+"F0.wireOp",EDGE,"E42.MirrorCS"),sQuery(id+"F0.wireOp",EDGE,"E38.MirrorCS"),sQuery(id+"F0.wireOp",EDGE,"E45.MirrorCS"),sQuery(id+"F0.wireOp",EDGE,"E39.MirrorCS"),sQuery(id+"F0.wireOp",EDGE,"E36.MirrorCS"),sQuery(id+"F0.wireOp",EDGE,"E41.MirrorCS"),sQuery(id+"F0.wireOp",EDGE,"E47.MirrorCS"),sQuery(id+"F0.wireOp",EDGE,"E44.MirrorCS"),sQuery(id+"F0.wireOp",EDGE,"E43.MirrorCS"),sQuery(id+"F0.wireOp",EDGE,"E40.MirrorCS"),sQuery(id+"F0.wireOp",EDGE,"E49.MirrorCS"),sQuery(id+"F0.wireOp",EDGE,"E48.MirrorCS"),sQuery(id+"F0.wireOp",EDGE,"E50.MirrorCS"),sQuery(id+"F0.wireOp",EDGE,"E51.MirrorCS"),sQuery(id+"F0.wireOp",EDGE,"E53.MirrorCS"),sQuery(id+"F0.wireOp",EDGE,"E57.MirrorCS"),sQuery(id+"F0.wireOp",EDGE,"E60.MirrorCS"),sQuery(id+"F0.wireOp",EDGE,"E63.MirrorCS"),sQuery(id+"F0.wireOp",EDGE,"E59.MirrorCS"),sQuery(id+"F0.wireOp",EDGE,"E58.MirrorCS"),sQuery(id+"F0.wireOp",EDGE,"E69.0.1.43"),sQuery(id+"F0.wireOp",EDGE,"E69.0.1.59"),sQuery(id+"F0.wireOp",EDGE,"E69.0.1.60"),sQuery(id+"F0.wireOp",EDGE,"E69.0.1.68"),sQuery(id+"F0.wireOp",EDGE,"E69.0.1.89"),sQuery(id+"F0.wireOp",EDGE,"E69.0.1.92"),sQuery(id+"F0.wireOp",EDGE,"E69.0.1.93"),sQuery(id+"F0.wireOp",EDGE,"E69.0.1.94"),sQuery(id+"F0.wireOp",EDGE,"E69.0.1.95"),sQuery(id+"F0.wireOp",EDGE,"E69.0.1.96"),sQuery(id+"F0.wireOp",EDGE,"E69.0.1.105"),sQuery(id+"F0.wireOp",EDGE,"E69.0.1.112"),sQuery(id+"F0.wireOp",EDGE,"E69.0.1.113"),sQuery(id+"F0.wireOp",EDGE,"E69.0.1.119"),sQuery(id+"F0.wireOp",EDGE,"E69.0.1.121"),sQuery(id+"F0.wireOp",EDGE,"E69.0.1.123"),sQuery(id+"F0.wireOp",EDGE,"E69.0.1.127"),sQuery(id+"F0.wireOp",EDGE,"E69.0.1.128"),sQuery(id+"F0.wireOp",EDGE,"E69.0.1.129"),sQuery(id+"F0.wireOp",EDGE,"E69.0.1.133"),sQuery(id+"F0.wireOp",EDGE,"E69.0.1.134"),sQuery(id+"F0.wireOp",EDGE,"E69.0.1.140"),sQuery(id+"F0.wireOp",EDGE,"E69.0.1.141"),sQuery(id+"F0.wireOp",EDGE,"E69.0.1.142"),sQuery(id+"F0.wireOp",EDGE,"E69.0.2.41"),sQuery(id+"F0.wireOp",EDGE,"E69.0.2.43"),sQuery(id+"F0.wireOp",EDGE,"E69.0.2.44"),sQuery(id+"F0.wireOp",EDGE,"E69.0.2.55"),sQuery(id+"F0.wireOp",EDGE,"E69.0.2.59"),sQuery(id+"F0.wireOp",EDGE,"E69.0.2.60"),sQuery(id+"F0.wireOp",EDGE,"E69.0.2.61"),sQuery(id+"F0.wireOp",EDGE,"E69.0.2.68"),sQuery(id+"F0.wireOp",EDGE,"E69.0.2.69"),sQuery(id+"F0.wireOp",EDGE,"E69.0.2.75"),sQuery(id+"F0.wireOp",EDGE,"E69.0.2.84"),sQuery(id+"F0.wireOp",EDGE,"E69.0.2.88"),sQuery(id+"F0.wireOp",EDGE,"E69.0.2.89"),sQuery(id+"F0.wireOp",EDGE,"E69.0.2.92"),sQuery(id+"F0.wireOp",EDGE,"E69.0.2.93"),sQuery(id+"F0.wireOp",EDGE,"E69.0.2.94"),sQuery(id+"F0.wireOp",EDGE,"E69.0.2.95"),sQuery(id+"F0.wireOp",EDGE,"E69.0.2.96"),sQuery(id+"F0.wireOp",EDGE,"E69.0.2.105"),sQuery(id+"F0.wireOp",EDGE,"E69.0.2.112"),sQuery(id+"F0.wireOp",EDGE,"E69.0.2.113"),sQuery(id+"F0.wireOp",EDGE,"E69.0.2.119"),sQuery(id+"F0.wireOp",EDGE,"E69.0.2.121"),sQuery(id+"F0.wireOp",EDGE,"E69.0.2.123"),sQuery(id+"F0.wireOp",EDGE,"E69.0.2.127"),sQuery(id+"F0.wireOp",EDGE,"E69.0.2.128"),sQuery(id+"F0.wireOp",EDGE,"E69.0.2.129"),sQuery(id+"F0.wireOp",EDGE,"E69.0.2.133"),sQuery(id+"F0.wireOp",EDGE,"E69.0.2.134"),sQuery(id+"F0.wireOp",EDGE,"E69.0.2.135"),sQuery(id+"F0.wireOp",EDGE,"E69.0.2.136"),sQuery(id+"F0.wireOp",EDGE,"E69.0.2.140"),sQuery(id+"F0.wireOp",EDGE,"E69.0.2.141"),sQuery(id+"F0.wireOp",EDGE,"E69.0.2.142"),sQuery(id+"F0.wireOp",EDGE,"E70.bottom"),sQuery(id+"F0.wireOp",EDGE,"E70.top"),sQuery(id+"F0.wireOp",EDGE,"E70.left"),sQuery(id+"F0.wireOp",EDGE,"E70.right")])],"isStart":false});
            var sketch = newSketch(context, id + "F10", { "sketchPlane" : qUnion([Q0])});
            skLineSegment(sketch, "E75", {"start": v(-9.65, -14.7) * mm, "end": v(12.73, -14.7) * mm});
            skPoint(sketch, "E76", {"position": v(0, -14.7) * mm});
            skSolve(sketch);
        }
        {
            var Q0;
            Q0=makeQuery(id+"F4.boolean.opBoolean","MERGE",FACE,{"derivedFrom":[makeQuery(id+"F1.opExtrude","SWEPT_FACE",FACE,{"disambiguationData":[OSD([sQuery(id+"F0.wireOp",EDGE,"E70.right")])]}),makeQuery(id+"F4.opExtrude","SWEPT_FACE",FACE,{"disambiguationData":[OSD([sQuery(id+"F3.wireOp",EDGE,"E71.left")])]})]});
            var sketch = newSketch(context, id + "F11", { "sketchPlane" : qUnion([Q0])});
            skPoint(sketch, "E77", {"position": v(-45.3, 46.86) * mm});
            skPoint(sketch, "E78", {"position": v(21.23, 7.49) * mm});
            skLineSegment(sketch, "E79.bottom", {"start": v(-78.18, 78.75) * mm, "end": v(49.74, 78.75) * mm});
            skLineSegment(sketch, "E79.top", {"start": v(-78.18, -52.5) * mm, "end": v(49.74, -52.5) * mm});
            skLineSegment(sketch, "E79.left", {"start": v(-78.18, 78.75) * mm, "end": v(-78.18, -52.5) * mm});
            skLineSegment(sketch, "E79.right", {"start": v(49.74, 78.75) * mm, "end": v(49.74, -52.5) * mm});
            skLineSegment(sketch, "E80.bottom", {"start": v(-51.61, 43.07) * mm, "end": v(24.59, 43.07) * mm});
            skLineSegment(sketch, "E80.top", {"start": v(-51.61, 3.7) * mm, "end": v(24.59, 3.7) * mm});
            skLineSegment(sketch, "E80.left", {"start": v(-51.61, 43.07) * mm, "end": v(-51.61, 3.7) * mm});
            skLineSegment(sketch, "E80.right", {"start": v(24.59, 43.07) * mm, "end": v(24.59, 3.7) * mm});
            skSolve(sketch);
        }
        {
            var Q0;
            Q0=qSketchRegion(id+"F11",true);
            extrude(context, id + "F12", {"entities" : qUnion([Q0]), "operationType" : NewBodyOperationType.REMOVE, "oppositeDirection" : true, "depth" : 76.2 * mm, "offsetDistance" : 25.4 * mm});
        }
        {
            var Q0;
            {var subQ2=sQuery(id+"F0.wireOp",EDGE,"E5");Q0=makeQuery(id+"F12.boolean.opBoolean","COPY",FACE,{"disambiguationData":[TD([makeQuery(id+"F1.opExtrude","SWEPT_FACE",FACE,{"disambiguationData":[OSD([subQ2])]})])],"derivedFrom":makeQuery(id+"F12.opExtrude","SWEPT_FACE",FACE,{"disambiguationData":[OSD([sQuery(id+"F11.wireOp",EDGE,"E80.top")])]})});}
            var sketch = newSketch(context, id + "F13", { "sketchPlane" : qUnion([Q0])});
            skLineSegment(sketch, "E81.bottom", {"start": v(-40.64, 27.96) * mm, "end": v(0, 27.96) * mm});
            skLineSegment(sketch, "E81.top", {"start": v(-40.64, -23.5) * mm, "end": v(0, -23.5) * mm});
            skLineSegment(sketch, "E81.left", {"start": v(-40.64, 27.96) * mm, "end": v(-40.64, -23.5) * mm});
            skLineSegment(sketch, "E81.right", {"start": v(0, 27.96) * mm, "end": v(0, -23.5) * mm});
            skSolve(sketch);
        }
        {
            var Q0;
            Q0=makeQuery(id+"F13.imprint","IMPRINT",FACE,{"disambiguationData":[TD([[makeQuery(id+"F13.imprint","IMPRINT",EDGE,{"derivedFrom":sQuery(id+"F13.wireOp",EDGE,"E81.top")}),-1.0]])]});
            var Q1;
            {var subQ0=makeQuery(id+"F12.opExtrude","SWEPT_FACE",FACE,{"disambiguationData":[OSD([sQuery(id+"F11.wireOp",EDGE,"E80.top")])]});var subQ2=makeQuery(id+"F12.boolean.opBoolean","INTERSECT",EDGE,{"derivedFrom":[makeQuery(id+"F1.opExtrude","SWEPT_FACE",FACE,{"disambiguationData":[OSD([sQuery(id+"F0.wireOp",EDGE,"E5")])]}),subQ0]});Q1=makeQuery(id+"F13.imprint","IMPRINT",FACE,{"disambiguationData":[TD([[makeQuery(id+"F13.imprint","IMPRINT",EDGE,{"derivedFrom":subQ2}),1.0]])]});}
            extrude(context, id + "F14", {"entities" : qUnion([Q0, Q1]), "operationType" : NewBodyOperationType.ADD, "depth" : 1.02 * mm, "offsetDistance" : 25.4 * mm});
        }
    });
